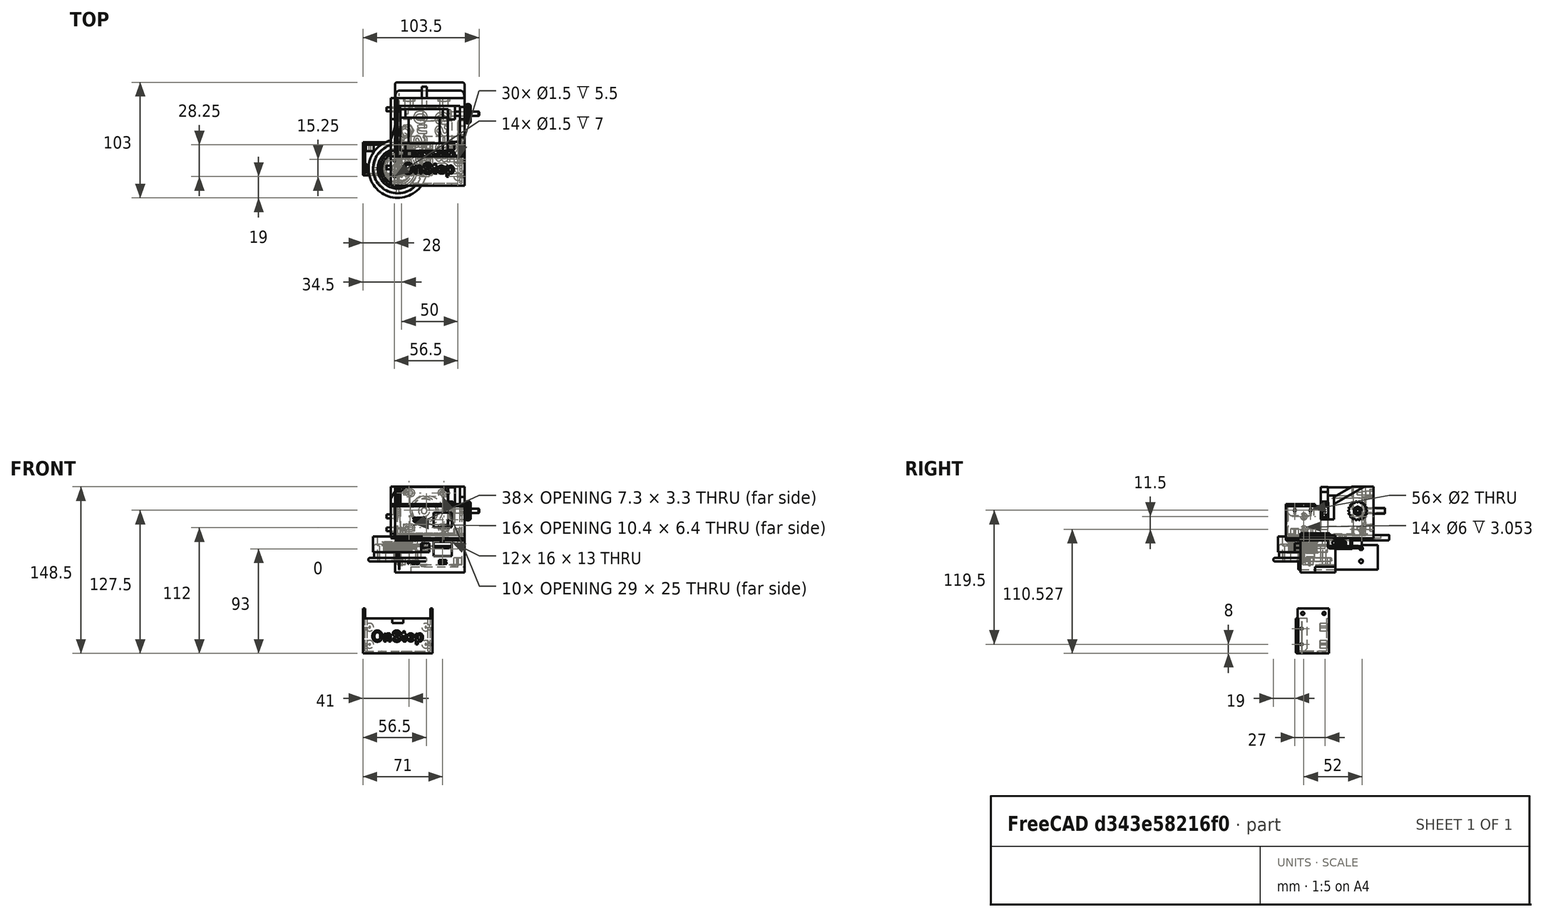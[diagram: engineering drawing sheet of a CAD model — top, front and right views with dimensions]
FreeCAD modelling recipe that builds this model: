
FCSTD DOCUMENT  (FreeCAD 0.17R13387 (Git))
Label: OnStep for GS280
License: All rights reserved
LicenseURL: http://en.wikipedia.org/wiki/All_rights_reserved
objects: Part::Cylinder×217, Part::Box×127, Part::MultiFuse×122, Part::Cut×53, Part::Feature×32, Part::Part2DObjectPython×21, Part::Extrusion×21, Part::FeaturePython×16, Part::Fillet×7, App::Part×6, Mesh::Feature×4, Part::Chamfer×3
note: 619 computed .brp shape members not serialized (recipe doc carries the construction recipe); baked Part::Feature solids carry a one-line shape summary decoded from their .brp

FEATURE [Part::Part2DObjectPython] ShapeString016  # Draft 2D object (typed FeaturePython)
  FontFile = <path>
  Placement = pos=(15.3452,-2,30.5072) rot=(1,0,0;1.5708rad)
  Size = 0.01
  String = .
  Tracking = 0
FEATURE [Part::Part2DObjectPython] ShapeString013  # Draft 2D object (typed FeaturePython)
  FontFile = <path>
  Placement = pos=(15.3452,-2,30.5072) rot=(1,0,0;1.5708rad)
  Size = 10
  String = OnStep
  Tracking = 0
FEATURE [Part::Part2DObjectPython] ShapeString017  # Draft 2D object (typed FeaturePython)
  FontFile = <path>
  Placement = pos=(15.3452,-2,30.5072) rot=(1,0,0;1.5708rad)
  Size = 4
  String = DEC
  Tracking = 0
FEATURE [Part::Cylinder] Cylinder014005703  label="Válec620"
  Angle = 360
  AttacherType = Attacher::AttachEngine3D
  Height = 70
  Placement = pos=(-5,6,16.5) rot=(0,1,0;1.5708rad)
  Radius = 1
FEATURE [Part::Box] Box159  label="Krychle136"
  AttacherType = Attacher::AttachEngine3D
  Height = 2
  Length = 62
  Placement = pos=(-2.5,-2,23) rot=(0,0,1;0rad)
  Width = 31
FEATURE [Part::Box] Box161  label="Krychle138"
  AttacherType = Attacher::AttachEngine3D
  Height = 8
  Length = 58
  Placement = pos=(-0.5,0,15) rot=(0,0,1;0rad)
  Width = 29
FEATURE [Part::MultiFuse] Fusion001071
  Shapes = -> [Box159,Box161]
FEATURE [Part::Box] Box158  label="Krychle135"
  AttacherType = Attacher::AttachEngine3D
  Height = 4
  Length = 10
  Placement = pos=(-5,-8,-55) rot=(0,0,1;0rad)
  Width = 5
FEATURE [Part::Extrusion] Extrude071  label="OnStep005"
  Base = -> ShapeString013
  Dir = (0,-1,0)
  DirMode = 2
  FaceMakerClass = Part::FaceMakerBullseye
  LengthFwd = 1
  LengthRev = 0
  Placement = pos=(-10,-22,22) rot=(-1,0,0;1.5708rad)
  Solid = false
  Symmetric = false
FEATURE [Part::Cylinder] Cylinder014005704  label="Válec621"
  Angle = 360
  AttacherType = Attacher::AttachEngine3D
  Height = 70
  Placement = pos=(-5,20,16.5) rot=(0,1,0;1.5708rad)
  Radius = 1
FEATURE [Part::MultiFuse] Fusion001073  label="Horni diry009"
  Placement = pos=(0,0,3) rot=(0,0,1;0rad)
  Shapes = -> [Cylinder014005704,Cylinder014005703]
FEATURE [Part::Box] Box160  label="Krychle137"
  AttacherType = Attacher::AttachEngine3D
  Height = 8
  Length = 54
  Placement = pos=(1.5,0,15) rot=(0,0,1;0rad)
  Width = 29
FEATURE [Part::MultiFuse] Fusion001072
  Shapes = -> [Fusion001073,Box160]
FEATURE [Part::Cut] Cut061098066
  Base = -> Fusion001071
  Tool = -> Fusion001072
FEATURE [Part::Cut] Cut061098067  label="viko s texty005"
  Base = -> Cut061098066
  Tool = -> Extrude071
FEATURE [Part::Chamfer] Chamfer008017
  Base = -> Cut061098067
  Edges = 2 edges r=2.5: [Edge355,Edge357]
FEATURE [Part::Fillet] Fillet009  label="DEC vicko003"
  Base = -> Chamfer008017
  Edges = 3 edges r=1: [Edge36,Edge38,Edge39]
  Placement = pos=(-28.5,19,-80) rot=(1,0,0;1.5708rad)
FEATURE [Part::Cut] Cut061098065  label="DEC PCB Cap"
  Base = -> Fillet009
  Tool = -> Box158
FEATURE [Part::Extrusion] Extrude086  label="Text RA002"
  Base = -> ShapeString017
  Dir = (0,-1,0)
  DirMode = 2
  FaceMakerClass = Part::FaceMakerBullseye
  LengthFwd = 1
  LengthRev = 0
  Placement = pos=(18,0.5,-33) rot=(0,0,1;0rad)
  Solid = false
  Symmetric = false
FEATURE [Part::Cylinder] Cylinder014005791  label="Válec704"
  Angle = 360
  AttacherType = Attacher::AttachEngine3D
  Height = 70
  Placement = pos=(-5,6,16.5) rot=(0,1,0;1.5708rad)
  Radius = 1
FEATURE [Part::Cylinder] Cylinder014005799  label="Válec712"
  Angle = 360
  AttacherType = Attacher::AttachEngine3D
  Height = 70
  Placement = pos=(-5,20,16.5) rot=(0,1,0;1.5708rad)
  Radius = 1
FEATURE [Part::Cylinder] Cylinder014005792  label="Válec705"
  Angle = 360
  AttacherType = Attacher::AttachEngine3D
  Height = 8
  Placement = pos=(53.5,21.25,0) rot=(0,0,1;0rad)
  Radius = 0.75
FEATURE [Part::Cylinder] Cylinder014005795  label="Válec708"
  Angle = 360
  AttacherType = Attacher::AttachEngine3D
  Height = 6.5
  Placement = pos=(53.5,6,0) rot=(0,0,1;0rad)
  Radius = 3.5
FEATURE [Part::Box] Box203  label="Krychle178"
  AttacherType = Attacher::AttachEngine3D
  Height = 13
  Length = 2
  Placement = pos=(-31,-4.5,-55) rot=(0,0,1;0rad)
  Width = 28
FEATURE [Part::Cylinder] Cylinder014005796  label="Válec709"
  Angle = 360
  AttacherType = Attacher::AttachEngine3D
  Height = 8
  Placement = pos=(53.5,6,0) rot=(0,0,1;0rad)
  Radius = 0.75
FEATURE [Part::Box] Box202  label="Krychle177"
  AttacherType = Attacher::AttachEngine3D
  Height = 13
  Length = 2
  Placement = pos=(29,-4.5,-55) rot=(0,0,1;0rad)
  Width = 28
FEATURE [Part::Box] Box201  label="RJ056"
  AttacherType = Attacher::AttachEngine3D
  Height = 13
  Length = 16
  Placement = pos=(32,-5,4.5) rot=(0,0,1;0rad)
  Width = 18.5
FEATURE [Part::Cylinder] Cylinder014005793  label="Válec706"
  Angle = 360
  AttacherType = Attacher::AttachEngine3D
  Height = 6.5
  Placement = pos=(3.5,21.25,0) rot=(0,0,1;0rad)
  Radius = 3.5
FEATURE [Part::Cylinder] Cylinder014005802  label="Válec715"
  Angle = 360
  AttacherType = Attacher::AttachEngine3D
  Height = 74
  Placement = pos=(-40,19,-46.5) rot=(0,1,0;1.5708rad)
  Radius = 1.4
FEATURE [Part::Box] Box204  label="Krychle179"
  AttacherType = Attacher::AttachEngine3D
  Height = 28
  Length = 62
  Placement = pos=(-2.5,-2,-5) rot=(0,0,1;0rad)
  Width = 31
FEATURE [Part::Box] Box200  label="Krychle176"
  AttacherType = Attacher::AttachEngine3D
  Height = 26
  Length = 58
  Placement = pos=(-0.5,0,-3) rot=(0,0,1;0rad)
  Width = 29
FEATURE [Part::Cut] Cut061098120  label="Základ002"
  Base = -> Box204
  Tool = -> Box200
FEATURE [Part::Extrusion] Extrude087  label="Text TR002"
  Base = -> ShapeString016
  Dir = (0,-1,0)
  DirMode = 2
  FaceMakerClass = Part::FaceMakerBullseye
  LengthFwd = 1
  LengthRev = 0
  Placement = pos=(-6.75,0.5,-33) rot=(0,0,1;0rad)
  Solid = false
  Symmetric = false
FEATURE [Part::Cylinder] Cylinder014005800  label="Válec713"
  Angle = 360
  AttacherType = Attacher::AttachEngine3D
  Height = 8
  Placement = pos=(3.5,21.25,0) rot=(0,0,1;0rad)
  Radius = 0.75
FEATURE [Part::Cylinder] Cylinder014005801  label="Válec714"
  Angle = 360
  AttacherType = Attacher::AttachEngine3D
  Height = 5
  Placement = pos=(14.25,1,9.5) rot=(1,0,0;1.5708rad)
  Radius = 0.01
FEATURE [Part::Cylinder] Cylinder014005803  label="Válec716"
  Angle = 360
  AttacherType = Attacher::AttachEngine3D
  Height = 74
  Placement = pos=(-40,0,-46.5) rot=(0,1,0;1.5708rad)
  Radius = 1.4
FEATURE [Part::Cylinder] Cylinder014005797  label="Válec710"
  Angle = 360
  AttacherType = Attacher::AttachEngine3D
  Height = 6.5
  Placement = pos=(53.5,21.25,0) rot=(0,0,1;0rad)
  Radius = 3.5
FEATURE [Part::Cylinder] Cylinder014005798  label="Válec711"
  Angle = 360
  AttacherType = Attacher::AttachEngine3D
  Height = 8
  Placement = pos=(3.5,6,0) rot=(0,0,1;0rad)
  Radius = 0.7
FEATURE [Part::Cylinder] Cylinder014005794  label="Válec707"
  Angle = 360
  AttacherType = Attacher::AttachEngine3D
  Height = 6.5
  Placement = pos=(3.5,6,0) rot=(0,0,1;0rad)
  Radius = 3.5
FEATURE [Part::MultiFuse] Fusion001089071  label="Horni diry011"
  Placement = pos=(0,0,3) rot=(0,0,1;0rad)
  Shapes = -> [Cylinder014005799,Cylinder014005791]
FEATURE [Part::MultiFuse] Fusion001089075
  Shapes = -> [Extrude087,Extrude086]
FEATURE [Part::MultiFuse] Fusion001089077
  Shapes = -> [Box202,Box203]
FEATURE [Part::MultiFuse] Fusion001089068  label="diry017"
  Placement = pos=(0,0,-4) rot=(0,0,1;0rad)
  Shapes = -> [Cylinder014005800,Cylinder014005798,Cylinder014005792,Cylinder014005796]
FEATURE [Part::MultiFuse] Fusion001089070  label="RJ a LED002"
  Shapes = -> [Box201,Cylinder014005801]
FEATURE [Part::MultiFuse] Fusion001089072  label="sloupky005"
  Placement = pos=(0,0,-3.5) rot=(0,0,1;0rad)
  Shapes = -> [Cylinder014005793,Cylinder014005794,Cylinder014005797,Cylinder014005795]
FEATURE [Part::MultiFuse] Fusion001089073
  Shapes = -> [Cylinder014005803,Cylinder014005802]
FEATURE [Part::MultiFuse] Fusion001089074  label="bez der002"
  Shapes = -> [Cut061098120,Fusion001089072]
FEATURE [Part::MultiFuse] Fusion001089069
  Shapes = -> [Fusion001089068,Fusion001089070,Fusion001089071]
FEATURE [Part::Cut] Cut061098121
  Base = -> Fusion001089074
  Tool = -> Fusion001089069
FEATURE [Part::Cut] Cut061098118
  Base = -> Cut061098121
  Placement = pos=(-28.5,18.5,-80) rot=(1,0,0;1.5708rad)
  Tool = -> Fusion001089075
FEATURE [Part::MultiFuse] Fusion001089076  label="RA pcb box002"
  Shapes = -> [Cut061098118,Fusion001089077]
FEATURE [Part::Cut] Cut061098119  label="DEC PCB BOX For MiniPCB2"
  Base = -> Fusion001089076
  Tool = -> Fusion001089073
FEATURE [Part::Feature] Cut061098127012  label="DE 012"
  shape: bbox 62 x 31 x 33 mm, 80 faces (baked)
FEATURE [Part::Fillet] Fillet004005002  label="DE final"
  Base = -> Cut061098127012
  Edges = 5 edges r=1: [Edge94,Edge95,Edge96,Edge97,Edge98]
FEATURE [Part::Feature] Cut005023015002001  label="RA PCB003"
  shape: bbox 62 x 31 x 33 mm, 145 faces (baked)
FEATURE [App::Part] Part
  Group = -> [Fusion001089075,Fusion001089068,Fusion001089076,Fusion001089077,Fusion001089070,Fusion001089074,Fusion001089069,Fusion001089071,Fusion001089072,Fusion001089073,Cut061098118,Cut061098121,Cut061098120,Cylinder014005802,Box201,Cylinder014005803,Cylinder014005799,Cylinder014005795,Box202,Cylinder014005793,Box203,Extrude086,Cylinder014005791,Box200,Cylinder014005800,Cylinder014005797,Cylinder014005794,+28 more]
  Origin = -> Origin
FEATURE [Mesh::Feature] support_nema17_EQ5_A_D__v1_1  label="support_nema17_EQ5_A.D._v1.1"
FEATURE [Mesh::Feature] support_nema17_EQ5_Dec_v1_1  label="support_nema17_EQ5_Dec_v1.1"
  Placement = pos=(-2,-2,13) rot=(0,0,1;0rad)
FEATURE [Mesh::Feature] holderDEC
  Placement = pos=(0,0,6) rot=(0,0,1;0rad)
FEATURE [Mesh::Feature] holderRA
FEATURE [Part::Feature] Pocket004
  Placement = pos=(22.5,32.5,13.5) rot=(0,0,1;1.5708rad)
  shape: bbox 61 x 74.5 x 11 mm, 39 faces (baked)
FEATURE [Part::Box] Box  label="Krychle"
  AttacherType = Attacher::AttachEngine3D
  Height = 43
  Length = 59.5
  Placement = pos=(0,56,23) rot=(0,0,1;0rad)
  Width = 7
FEATURE [Part::Box] Box205  label="Krychle180"
  AttacherType = Attacher::AttachEngine3D
  Height = 43
  Length = 43
  Placement = pos=(2,53,23) rot=(0,0,1;0rad)
  Width = 3
FEATURE [Part::Cylinder] Cylinder014005804  label="Válec717"
  Angle = 360
  AttacherType = Attacher::AttachEngine3D
  Height = 10
  Placement = pos=(8,57,29.5) rot=(1,0,0;1.5708rad)
  Radius = 1.65
FEATURE [Part::Cylinder] Cylinder014005805  label="Válec718"
  Angle = 360
  AttacherType = Attacher::AttachEngine3D
  Height = 10
  Placement = pos=(39,57,60.5) rot=(1,0,0;1.5708rad)
  Radius = 1.65
FEATURE [Part::Cylinder] Cylinder014005806  label="Válec719"
  Angle = 360
  AttacherType = Attacher::AttachEngine3D
  Height = 10
  Placement = pos=(39,57,29.5) rot=(1,0,0;1.5708rad)
  Radius = 1.65
FEATURE [Part::Cylinder] Cylinder014005807  label="Válec720"
  Angle = 360
  AttacherType = Attacher::AttachEngine3D
  Height = 10
  Placement = pos=(8,57,60.5) rot=(1,0,0;1.5708rad)
  Radius = 1.65
FEATURE [Part::Cylinder] Cylinder014005808  label="Válec721"
  Angle = 360
  AttacherType = Attacher::AttachEngine3D
  Height = 10
  Placement = pos=(23.5,59,45) rot=(1,0,0;1.5708rad)
  Radius = 12.5
FEATURE [Part::Box] Box206  label="Krychle181"
  AttacherType = Attacher::AttachEngine3D
  Height = 43
  Length = 6
  Placement = pos=(45,44,23) rot=(0,0,1;0rad)
  Width = 12
FEATURE [Part::FeaturePython] Screw010  label="M4x25-Screw001"  # Fasteners workbench fastener (typed FeaturePython)
  Placement = pos=(47.5,49,45) rot=(0,-1,0;1.5708rad)
  diameter = 6
  invert = false
  length = 0
  matchOuter = false
  offset = 0
  thread = false
  type = 13
FEATURE [Part::MultiFuse] Fusion  label="diry jezdec"
  Shapes = -> [Cylinder014005804,Cylinder014005808,Cylinder014005807,Cylinder014005806,Cylinder014005805,Screw010]
FEATURE [Part::MultiFuse] Fusion001089078
  Shapes = -> [Box205,Box206]
FEATURE [Part::Cut] Cut  label="Jezdec"
  Base = -> Fusion001089078
  Tool = -> Fusion
FEATURE [Part::Cylinder] Cylinder014005809  label="Válec722"
  Angle = 360
  AttacherType = Attacher::AttachEngine3D
  Height = 20
  Placement = pos=(23.5,64,45) rot=(1,0,0;1.5708rad)
  Radius = 12.5
FEATURE [Part::Cylinder] Cylinder014005810  label="Válec723"
  Angle = 360
  AttacherType = Attacher::AttachEngine3D
  Height = 10
  Placement = pos=(8,64,29.5) rot=(1,0,0;1.5708rad)
  Radius = 1.65
FEATURE [Part::Cylinder] Cylinder014005811  label="Válec724"
  Angle = 360
  AttacherType = Attacher::AttachEngine3D
  Height = 10
  Placement = pos=(8,64,60.5) rot=(1,0,0;1.5708rad)
  Radius = 1.65
FEATURE [Part::Cylinder] Cylinder014005812  label="Válec725"
  Angle = 360
  AttacherType = Attacher::AttachEngine3D
  Height = 10
  Placement = pos=(39,64,29.5) rot=(1,0,0;1.5708rad)
  Radius = 1.65
FEATURE [Part::Cylinder] Cylinder014005813  label="Válec726"
  Angle = 360
  AttacherType = Attacher::AttachEngine3D
  Height = 10
  Placement = pos=(39,64,60.5) rot=(1,0,0;1.5708rad)
  Radius = 1.65
FEATURE [Part::FeaturePython] Screw011  label="M4x25-Screw002"  # Fasteners workbench fastener (typed FeaturePython)
  Placement = pos=(47.5,49,45) rot=(0,-1,0;1.5708rad)
  diameter = 6
  invert = false
  length = 0
  matchOuter = false
  offset = 0
  thread = false
  type = 13
FEATURE [Part::Box] Box207  label="Krychle182"
  AttacherType = Attacher::AttachEngine3D
  Height = 43
  Length = 4
  Placement = pos=(55.5,16,23) rot=(0,0,1;0rad)
  Width = 40
FEATURE [Part::Cylinder] Cylinder014005814  label="Válec727"
  Angle = 360
  AttacherType = Attacher::AttachEngine3D
  Height = 10
  Placement = pos=(8,64,29.5) rot=(1,0,0;1.5708rad)
  Radius = 1.65
FEATURE [Part::Cylinder] Cylinder014005815  label="Válec728"
  Angle = 360
  AttacherType = Attacher::AttachEngine3D
  Height = 20
  Placement = pos=(23.5,64,45) rot=(1,0,0;1.5708rad)
  Radius = 12.5
FEATURE [Part::Cylinder] Cylinder014005816  label="Válec729"
  Angle = 360
  AttacherType = Attacher::AttachEngine3D
  Height = 10
  Placement = pos=(8,64,60.5) rot=(1,0,0;1.5708rad)
  Radius = 1.65
FEATURE [Part::Cylinder] Cylinder014005817  label="Válec730"
  Angle = 360
  AttacherType = Attacher::AttachEngine3D
  Height = 10
  Placement = pos=(39,64,29.5) rot=(1,0,0;1.5708rad)
  Radius = 1.65
FEATURE [Part::Cylinder] Cylinder014005818  label="Válec731"
  Angle = 360
  AttacherType = Attacher::AttachEngine3D
  Height = 10
  Placement = pos=(39,64,60.5) rot=(1,0,0;1.5708rad)
  Radius = 1.65
FEATURE [Part::MultiFuse] Fusion001089080
  Placement = pos=(4,0,0) rot=(0,0,1;0rad)
  Shapes = -> [Cylinder014005814,Cylinder014005816,Cylinder014005818,Cylinder014005815,Cylinder014005817]
FEATURE [Part::Box] Box208  label="Krychle183"
  AttacherType = Attacher::AttachEngine3D
  Height = 25
  Length = 4
  Placement = pos=(23.5,56,32.5) rot=(0,0,1;0rad)
  Width = 8
FEATURE [Part::Box] Box209  label="Krychle184"
  AttacherType = Attacher::AttachEngine3D
  Height = 3.3
  Length = 4
  Placement = pos=(8,56,27.85) rot=(0,0,1;0rad)
  Width = 8
FEATURE [Part::Box] Box210  label="Krychle185"
  AttacherType = Attacher::AttachEngine3D
  Height = 3.3
  Length = 4
  Placement = pos=(39,56,58.85) rot=(0,0,1;0rad)
  Width = 8
FEATURE [Part::Box] Box211  label="Krychle186"
  AttacherType = Attacher::AttachEngine3D
  Height = 3.3
  Length = 4
  Placement = pos=(39,56,27.85) rot=(0,0,1;0rad)
  Width = 8
FEATURE [Part::Box] Box212  label="Krychle187"
  AttacherType = Attacher::AttachEngine3D
  Height = 3.3
  Length = 4
  Placement = pos=(8,56,58.85) rot=(0,0,1;0rad)
  Width = 8
FEATURE [Part::MultiFuse] Fusion001089081  label="Main"
  Placement = pos=(0,0,0.5) rot=(0,0,1;0rad)
  Shapes = -> [Box,Box207]
FEATURE [Part::Box] Box213  label="konektor"
  AttacherType = Attacher::AttachEngine3D
  Height = 29
  Length = 10
  Placement = pos=(50,16,37) rot=(0,0,1;0rad)
  Width = 12
FEATURE [Part::Box] Box214  label="Krychle188"
  AttacherType = Attacher::AttachEngine3D
  Height = 43
  Length = 4
  Placement = pos=(55.5,22,47) rot=(1,0,0;0.523599rad)
  Width = 40
FEATURE [Part::MultiFuse] Fusion001089079  label="diry"
  Placement = pos=(0,0,0.5) rot=(0,0,1;0rad)
  Shapes = -> [Cylinder014005810,Cylinder014005809,Cylinder014005811,Cylinder014005812,Cylinder014005813,Screw011,Fusion001089080,Box208,Box209,Box210,Box211,Box212,Box213,Box214]
FEATURE [Part::Cut] Cut005023015002002  label="RA"
  Base = -> Fusion001089081
  Tool = -> Fusion001089079
FEATURE [Part::Part2DObjectPython] ShapeString015  # Draft 2D object (typed FeaturePython)
  FontFile = <path>
  Placement = pos=(15.3452,-2,30.5072) rot=(1,0,0;1.5708rad)
  Size = 0.01
  String = .
  Tracking = 0
FEATURE [Part::Part2DObjectPython] ShapeString014  # Draft 2D object (typed FeaturePython)
  FontFile = <path>
  Placement = pos=(15.3452,-2,30.5072) rot=(1,0,0;1.5708rad)
  Size = 4
  String = RA
  Tracking = 0
FEATURE [Part::Cylinder] Cylinder014005783  label="Válec696"
  Angle = 360
  AttacherType = Attacher::AttachEngine3D
  Height = 70
  Placement = pos=(-5,20,16.5) rot=(0,1,0;1.5708rad)
  Radius = 1
FEATURE [Part::Extrusion] Extrude084  label="Text RA001"
  Base = -> ShapeString014
  Dir = (0,-1,0)
  DirMode = 2
  FaceMakerClass = Part::FaceMakerBullseye
  LengthFwd = 1
  LengthRev = 0
  Placement = pos=(4,0.7,-23.5) rot=(0,0,1;0rad)
  Solid = false
  Symmetric = false
FEATURE [Part::Cylinder] Cylinder014005778  label="Válec691"
  Angle = 360
  AttacherType = Attacher::AttachEngine3D
  Height = 8
  Placement = pos=(3.5,6,0) rot=(0,0,1;0rad)
  Radius = 0.7
FEATURE [Part::Cylinder] Cylinder014005779  label="Válec692"
  Angle = 360
  AttacherType = Attacher::AttachEngine3D
  Height = 8
  Placement = pos=(53.5,21.25,0) rot=(0,0,1;0rad)
  Radius = 0.75
FEATURE [Part::Cylinder] Cylinder014005780  label="Válec693"
  Angle = 360
  AttacherType = Attacher::AttachEngine3D
  Height = 6.5
  Placement = pos=(3.5,6,0) rot=(0,0,1;0rad)
  Radius = 3.5
FEATURE [Part::Box] Box195  label="Krychle172"
  AttacherType = Attacher::AttachEngine3D
  Height = 26
  Length = 58
  Placement = pos=(-0.5,0,-3) rot=(0,0,1;0rad)
  Width = 29
FEATURE [Part::Cylinder] Cylinder014005781  label="Válec694"
  Angle = 360
  AttacherType = Attacher::AttachEngine3D
  Height = 6.5
  Placement = pos=(53.5,21.25,0) rot=(0,0,1;0rad)
  Radius = 3.5
FEATURE [Part::Cylinder] Cylinder014005782  label="Válec695"
  Angle = 360
  AttacherType = Attacher::AttachEngine3D
  Height = 8
  Placement = pos=(53.5,6,0) rot=(0,0,1;0rad)
  Radius = 0.75
FEATURE [Part::Cylinder] Cylinder014005784  label="Válec697"
  Angle = 360
  AttacherType = Attacher::AttachEngine3D
  Height = 70
  Placement = pos=(-5,6,16.5) rot=(0,1,0;1.5708rad)
  Radius = 1
FEATURE [Part::Box] Box196  label="RJ055"
  AttacherType = Attacher::AttachEngine3D
  Height = 13
  Length = 16
  Placement = pos=(32,-5,4.5) rot=(0,0,1;0rad)
  Width = 18.5
FEATURE [Part::Cylinder] Cylinder014005786  label="Válec699"
  Angle = 360
  AttacherType = Attacher::AttachEngine3D
  Height = 8
  Placement = pos=(3.5,21.25,0) rot=(0,0,1;0rad)
  Radius = 0.75
FEATURE [Part::Cylinder] Cylinder014005787  label="Válec700"
  Angle = 360
  AttacherType = Attacher::AttachEngine3D
  Height = 6.5
  Placement = pos=(3.5,21.25,0) rot=(0,0,1;0rad)
  Radius = 3.5
FEATURE [Part::Cylinder] Cylinder014005785  label="Válec698"
  Angle = 360
  AttacherType = Attacher::AttachEngine3D
  Height = 5
  Placement = pos=(14.25,1,9.5) rot=(1,0,0;1.5708rad)
  Radius = 0.01
FEATURE [Part::Cylinder] Cylinder014005788  label="Válec701"
  Angle = 360
  AttacherType = Attacher::AttachEngine3D
  Height = 6.5
  Placement = pos=(53.5,6,0) rot=(0,0,1;0rad)
  Radius = 3.5
FEATURE [Part::Box] Box199  label="Krychle175"
  AttacherType = Attacher::AttachEngine3D
  Height = 28
  Length = 62
  Placement = pos=(-2.5,-2,-5) rot=(0,0,1;0rad)
  Width = 31
FEATURE [Part::Cut] Cut061098114  label="Základ001"
  Base = -> Box199
  Tool = -> Box195
FEATURE [Part::Extrusion] Extrude085  label="Text TR001"
  Base = -> ShapeString015
  Dir = (0,-1,0)
  DirMode = 2
  FaceMakerClass = Part::FaceMakerBullseye
  LengthFwd = 1
  LengthRev = 0
  Placement = pos=(-6.75,1,-33) rot=(0,0,1;0rad)
  Solid = false
  Symmetric = false
FEATURE [Part::MultiFuse] Fusion001089063
  Shapes = -> [Extrude085,Extrude084]
FEATURE [Part::MultiFuse] Fusion001089058  label="RJ a LED001"
  Shapes = -> [Box196,Cylinder014005785]
FEATURE [Part::MultiFuse] Fusion001089059  label="Horni diry010"
  Placement = pos=(0,0,3) rot=(0,0,1;0rad)
  Shapes = -> [Cylinder014005783,Cylinder014005784]
FEATURE [Part::MultiFuse] Fusion001089060  label="diry016"
  Placement = pos=(0,0,-4) rot=(0,0,1;0rad)
  Shapes = -> [Cylinder014005786,Cylinder014005778,Cylinder014005779,Cylinder014005782]
FEATURE [Part::MultiFuse] Fusion001089062
  Shapes = -> [Fusion001089060,Fusion001089058,Fusion001089059]
FEATURE [Part::MultiFuse] Fusion001089061  label="sloupky004"
  Placement = pos=(0,0,-3.5) rot=(0,0,1;0rad)
  Shapes = -> [Cylinder014005787,Cylinder014005780,Cylinder014005781,Cylinder014005788]
FEATURE [Part::MultiFuse] Fusion001089067  label="bez der001"
  Shapes = -> [Cut061098114,Fusion001089061]
FEATURE [Part::Cut] Cut061098117
  Base = -> Fusion001089067
  Tool = -> Fusion001089062
FEATURE [Part::Cut] Cut061098115  label="PCB"
  Base = -> Cut061098117
  Placement = pos=(0,-13,26) rot=(1,0,0;0rad)
  Tool = -> Fusion001089063
FEATURE [Part::Box] Box215  label="Krychle189"
  AttacherType = Attacher::AttachEngine3D
  Height = 3
  Length = 62
  Placement = pos=(-2.5,-15,20.5) rot=(0,0,1;0rad)
  Width = 78
FEATURE [Part::Box] Box216  label="Krychle190"
  AttacherType = Attacher::AttachEngine3D
  Height = 8
  Length = 24
  Placement = pos=(-1.5,12.5,13.5) rot=(0,0,1;0rad)
  Width = 40
FEATURE [Part::Box] Box217  label="Krychle191"
  AttacherType = Attacher::AttachEngine3D
  Height = 8
  Length = 26
  Placement = pos=(22.5,22.5,13.5) rot=(0,0,1;0rad)
  Width = 20
FEATURE [Part::Box] Box218  label="Krychle192"
  AttacherType = Attacher::AttachEngine3D
  Height = 8
  Length = 6
  Placement = pos=(53.5,22.5,13.5) rot=(0,0,1;0rad)
  Width = 20
FEATURE [Part::MultiFuse] Fusion001089082  label="spodek"
  Shapes = -> [Box215,Box218,Box216,Box217]
FEATURE [Part::FeaturePython] Screw  label="M6x12-Screw"  # Fasteners workbench fastener (typed FeaturePython)
  Placement = pos=(6.5,32.5,19.5) rot=(1,0,0;0rad)
  diameter = 8
  invert = false
  length = 0
  matchOuter = false
  offset = 0
  thread = false
  type = 14
FEATURE [Part::Cylinder] Cylinder  label="Válec"
  Angle = 360
  AttacherType = Attacher::AttachEngine3D
  Height = 10
  Placement = pos=(52,28,16.5) rot=(0,1,0;1.5708rad)
  Radius = 1.65
FEATURE [Part::Cylinder] Cylinder014005819  label="Válec732"
  Angle = 360
  AttacherType = Attacher::AttachEngine3D
  Height = 10
  Placement = pos=(52,37,16.5) rot=(0,1,0;1.5708rad)
  Radius = 1.65
FEATURE [Part::Box] Box219  label="Krychle193"
  AttacherType = Attacher::AttachEngine3D
  Height = 3.3
  Length = 10
  Placement = pos=(52,28,14.85) rot=(0,0,1;0rad)
  Width = 9
FEATURE [Part::MultiFuse] Fusion001089083  label="Diryspodek"
  Shapes = -> [Box219,Cylinder,Cylinder014005819,Screw]
FEATURE [Part::Cut] Cut005023015002003  label="Spodek"
  Base = -> Fusion001089082
  Tool = -> Fusion001089083
FEATURE [Part::MultiFuse] Fusion001089084
  Shapes = -> [Cut061098115,Cut005023015002003,Cut005023015002002]
FEATURE [Part::FeaturePython] Screw012  label="M4x25-Screw003"  # Fasteners workbench fastener (typed FeaturePython)
  Placement = pos=(47.5,49,45) rot=(0,-1,0;1.5708rad)
  diameter = 6
  invert = false
  length = 0
  matchOuter = false
  offset = 0
  thread = false
  type = 13
FEATURE [Part::FeaturePython] Screw013  label="M6x12-Screw001"  # Fasteners workbench fastener (typed FeaturePython)
  Placement = pos=(8.5,34,19.5) rot=(1,0,0;0rad)
  diameter = 8
  invert = false
  length = 0
  matchOuter = false
  offset = 0
  thread = false
  type = 14
FEATURE [Part::Cylinder] Cylinder014005820  label="Válec733"
  Angle = 360
  AttacherType = Attacher::AttachEngine3D
  Height = 10
  Placement = pos=(8,64,60.5) rot=(1,0,0;1.5708rad)
  Radius = 1.65
FEATURE [Part::Cylinder] Cylinder014005821  label="Válec734"
  Angle = 360
  AttacherType = Attacher::AttachEngine3D
  Height = 10
  Placement = pos=(39,64,29.5) rot=(1,0,0;1.5708rad)
  Radius = 1.65
FEATURE [Part::Cylinder] Cylinder014005822  label="Válec735"
  Angle = 360
  AttacherType = Attacher::AttachEngine3D
  Height = 10
  Placement = pos=(8,64,60.5) rot=(1,0,0;1.5708rad)
  Radius = 1.65
FEATURE [Part::Cylinder] Cylinder014005823  label="Válec736"
  Angle = 360
  AttacherType = Attacher::AttachEngine3D
  Height = 10
  Placement = pos=(8,64,29.5) rot=(1,0,0;1.5708rad)
  Radius = 1.65
FEATURE [Part::Cylinder] Cylinder014005824  label="Válec737"
  Angle = 360
  AttacherType = Attacher::AttachEngine3D
  Height = 10
  Placement = pos=(39,64,29.5) rot=(1,0,0;1.5708rad)
  Radius = 1.65
FEATURE [Part::Box] Box220  label="Krychle194"
  AttacherType = Attacher::AttachEngine3D
  Height = 43
  Length = 59.5
  Placement = pos=(0,56,23) rot=(0,0,1;0rad)
  Width = 7
FEATURE [Part::Box] Box221  label="Krychle195"
  AttacherType = Attacher::AttachEngine3D
  Height = 43
  Length = 4
  Placement = pos=(55.5,16,23) rot=(0,0,1;0rad)
  Width = 40
FEATURE [Part::Cylinder] Cylinder014005825  label="Válec738"
  Angle = 360
  AttacherType = Attacher::AttachEngine3D
  Height = 20
  Placement = pos=(23.5,64,45) rot=(1,0,0;1.5708rad)
  Radius = 12.5
FEATURE [Part::Cylinder] Cylinder014005826  label="Válec739"
  Angle = 360
  AttacherType = Attacher::AttachEngine3D
  Height = 10
  Placement = pos=(39,64,60.5) rot=(1,0,0;1.5708rad)
  Radius = 1.65
FEATURE [Part::Cylinder] Cylinder014005827  label="Válec740"
  Angle = 360
  AttacherType = Attacher::AttachEngine3D
  Height = 10
  Placement = pos=(8,64,29.5) rot=(1,0,0;1.5708rad)
  Radius = 1.65
FEATURE [Part::Cylinder] Cylinder014005828  label="Válec741"
  Angle = 360
  AttacherType = Attacher::AttachEngine3D
  Height = 20
  Placement = pos=(23.5,64,45) rot=(1,0,0;1.5708rad)
  Radius = 12.5
FEATURE [Part::MultiFuse] Fusion001089085  label="Main001"
  Placement = pos=(0,0,0.5) rot=(0,0,1;0rad)
  Shapes = -> [Box220,Box221]
FEATURE [Part::Cylinder] Cylinder014005829  label="Válec742"
  Angle = 360
  AttacherType = Attacher::AttachEngine3D
  Height = 10
  Placement = pos=(39,64,60.5) rot=(1,0,0;1.5708rad)
  Radius = 1.65
FEATURE [Part::MultiFuse] Fusion001089090
  Placement = pos=(4,0,0) rot=(0,0,1;0rad)
  Shapes = -> [Cylinder014005827,Cylinder014005820,Cylinder014005829,Cylinder014005828,Cylinder014005821]
FEATURE [Part::Box] Box224  label="Krychle198"
  AttacherType = Attacher::AttachEngine3D
  Height = 9
  Length = 26
  Placement = pos=(-2,24,13) rot=(0,0,1;0rad)
  Width = 20
FEATURE [Part::Box] Box225  label="Krychle199"
  AttacherType = Attacher::AttachEngine3D
  Height = 25
  Length = 4
  Placement = pos=(23.5,56,32.5) rot=(0,0,1;0rad)
  Width = 8
FEATURE [Part::Box] Box226  label="Krychle200"
  AttacherType = Attacher::AttachEngine3D
  Height = 3.3
  Length = 4
  Placement = pos=(39,56,58.85) rot=(0,0,1;0rad)
  Width = 8
FEATURE [Part::Box] Box227  label="Krychle201"
  AttacherType = Attacher::AttachEngine3D
  Height = 43
  Length = 4
  Placement = pos=(55.5,22,47) rot=(1,0,0;0.523599rad)
  Width = 40
FEATURE [Part::Box] Box228  label="konektor001"
  AttacherType = Attacher::AttachEngine3D
  Height = 29
  Length = 10
  Placement = pos=(50,16,37) rot=(0,0,1;0rad)
  Width = 12
FEATURE [Part::Box] Box229  label="Krychle202"
  AttacherType = Attacher::AttachEngine3D
  Height = 3.3
  Length = 4
  Placement = pos=(39,56,27.85) rot=(0,0,1;0rad)
  Width = 8
FEATURE [Part::Box] Box230  label="Krychle203"
  AttacherType = Attacher::AttachEngine3D
  Height = 3.3
  Length = 4
  Placement = pos=(8,56,27.85) rot=(0,0,1;0rad)
  Width = 8
FEATURE [Part::Box] Box232  label="Krychle204"
  AttacherType = Attacher::AttachEngine3D
  Height = 3
  Length = 62
  Placement = pos=(-2.5,-15,20.5) rot=(0,0,1;0rad)
  Width = 78
FEATURE [Part::MultiFuse] Fusion001089088  label="spodek001"
  Shapes = -> [Box232,Box224]
FEATURE [Part::Box] Box233  label="Krychle205"
  AttacherType = Attacher::AttachEngine3D
  Height = 3.3
  Length = 4
  Placement = pos=(8,56,58.85) rot=(0,0,1;0rad)
  Width = 8
FEATURE [Part::MultiFuse] Fusion001089091  label="diry018"
  Placement = pos=(0,0,0.5) rot=(0,0,1;0rad)
  Shapes = -> [Cylinder014005823,Cylinder014005825,Cylinder014005822,Cylinder014005824,Cylinder014005826,Screw012,Fusion001089090,Box225,Box230,Box226,Box229,Box233,Box228,Box227]
FEATURE [Part::Cut] Cut005023015002008  label="DEC"
  Base = -> Fusion001089085
  Tool = -> Fusion001089091
FEATURE [Part::Cut] Cut005023015002009  label="dec spodek"
  Base = -> Fusion001089088
  Tool = -> Screw013
FEATURE [Part::Part2DObjectPython] ShapeString018  # Draft 2D object (typed FeaturePython)
  FontFile = <path>
  Placement = pos=(15.3452,-2,30.5072) rot=(1,0,0;1.5708rad)
  Size = 4
  String = DEC
  Tracking = 0
FEATURE [Part::Part2DObjectPython] ShapeString019  # Draft 2D object (typed FeaturePython)
  FontFile = <path>
  Placement = pos=(15.3452,-2,30.5072) rot=(1,0,0;1.5708rad)
  Size = 0.01
  String = .
  Tracking = 0
FEATURE [Part::Box] Box234  label="Krychle206"
  AttacherType = Attacher::AttachEngine3D
  Height = 26
  Length = 58
  Placement = pos=(-0.5,0,-3) rot=(0,0,1;0rad)
  Width = 29
FEATURE [Part::Box] Box235  label="Krychle207"
  AttacherType = Attacher::AttachEngine3D
  Height = 28
  Length = 62
  Placement = pos=(-2.5,-2,-5) rot=(0,0,1;0rad)
  Width = 31
FEATURE [Part::Cut] Cut005023015002010  label="Základ003"
  Base = -> Box235
  Tool = -> Box234
FEATURE [Part::Cylinder] Cylinder014005830  label="Válec743"
  Angle = 360
  AttacherType = Attacher::AttachEngine3D
  Height = 70
  Placement = pos=(-5,20,16.5) rot=(0,1,0;1.5708rad)
  Radius = 1
FEATURE [Part::Extrusion] Extrude088  label="Text TR003"
  Base = -> ShapeString019
  Dir = (0,-1,0)
  DirMode = 2
  FaceMakerClass = Part::FaceMakerBullseye
  LengthFwd = 1
  LengthRev = 0
  Placement = pos=(-6.75,0.5,-33) rot=(0,0,1;0rad)
  Solid = false
  Symmetric = false
FEATURE [Part::Cylinder] Cylinder014005831  label="Válec744"
  Angle = 360
  AttacherType = Attacher::AttachEngine3D
  Height = 8
  Placement = pos=(3.5,6,0) rot=(0,0,1;0rad)
  Radius = 0.7
FEATURE [Part::Cylinder] Cylinder014005832  label="Válec745"
  Angle = 360
  AttacherType = Attacher::AttachEngine3D
  Height = 8
  Placement = pos=(53.5,21.25,0) rot=(0,0,1;0rad)
  Radius = 0.75
FEATURE [Part::Cylinder] Cylinder014005833  label="Válec746"
  Angle = 360
  AttacherType = Attacher::AttachEngine3D
  Height = 6.5
  Placement = pos=(3.5,6,0) rot=(0,0,1;0rad)
  Radius = 3.5
FEATURE [Part::Cylinder] Cylinder014005834  label="Válec747"
  Angle = 360
  AttacherType = Attacher::AttachEngine3D
  Height = 6.5
  Placement = pos=(53.5,21.25,0) rot=(0,0,1;0rad)
  Radius = 3.5
FEATURE [Part::Cylinder] Cylinder014005835  label="Válec748"
  Angle = 360
  AttacherType = Attacher::AttachEngine3D
  Height = 8
  Placement = pos=(53.5,6,0) rot=(0,0,1;0rad)
  Radius = 0.75
FEATURE [Part::Cylinder] Cylinder014005836  label="Válec749"
  Angle = 360
  AttacherType = Attacher::AttachEngine3D
  Height = 70
  Placement = pos=(-5,6,16.5) rot=(0,1,0;1.5708rad)
  Radius = 1
FEATURE [Part::MultiFuse] Fusion001089097  label="Horni diry012"
  Placement = pos=(0,0,3) rot=(0,0,1;0rad)
  Shapes = -> [Cylinder014005830,Cylinder014005836]
FEATURE [Part::Extrusion] Extrude089  label="Text RA003"
  Base = -> ShapeString018
  Dir = (0,-1,0)
  DirMode = 2
  FaceMakerClass = Part::FaceMakerBullseye
  LengthFwd = 1
  LengthRev = 0
  Placement = pos=(40,1,43.5) rot=(0,1,0;3.14159rad)
  Solid = false
  Symmetric = false
FEATURE [Part::MultiFuse] Fusion001089095
  Shapes = -> [Extrude088,Extrude089]
FEATURE [Part::Box] Box236  label="RJ057"
  AttacherType = Attacher::AttachEngine3D
  Height = 13
  Length = 16
  Placement = pos=(32,-5,4.5) rot=(0,0,1;0rad)
  Width = 18.5
FEATURE [Part::Cylinder] Cylinder014005837  label="Válec750"
  Angle = 360
  AttacherType = Attacher::AttachEngine3D
  Height = 8
  Placement = pos=(3.5,21.25,0) rot=(0,0,1;0rad)
  Radius = 0.75
FEATURE [Part::MultiFuse] Fusion001089098  label="diry019"
  Placement = pos=(0,0,-4) rot=(0,0,1;0rad)
  Shapes = -> [Cylinder014005837,Cylinder014005831,Cylinder014005832,Cylinder014005835]
FEATURE [Part::Cylinder] Cylinder014005838  label="Válec751"
  Angle = 360
  AttacherType = Attacher::AttachEngine3D
  Height = 6.5
  Placement = pos=(3.5,21.25,0) rot=(0,0,1;0rad)
  Radius = 3.5
FEATURE [Part::Cylinder] Cylinder014005839  label="Válec752"
  Angle = 360
  AttacherType = Attacher::AttachEngine3D
  Height = 5
  Placement = pos=(14.25,1,9.5) rot=(1,0,0;1.5708rad)
  Radius = 0.01
FEATURE [Part::MultiFuse] Fusion001089096  label="RJ a LED003"
  Shapes = -> [Box236,Cylinder014005839]
FEATURE [Part::MultiFuse] Fusion001089092
  Shapes = -> [Fusion001089098,Fusion001089096,Fusion001089097]
FEATURE [Part::Cylinder] Cylinder014005840  label="Válec753"
  Angle = 360
  AttacherType = Attacher::AttachEngine3D
  Height = 6.5
  Placement = pos=(53.5,6,0) rot=(0,0,1;0rad)
  Radius = 3.5
FEATURE [Part::MultiFuse] Fusion001089093  label="sloupky006"
  Placement = pos=(0,0,-3.5) rot=(0,0,1;0rad)
  Shapes = -> [Cylinder014005838,Cylinder014005833,Cylinder014005834,Cylinder014005840]
FEATURE [Part::MultiFuse] Fusion001089094  label="bez der003"
  Shapes = -> [Cut005023015002010,Fusion001089093]
FEATURE [Part::Cut] Cut005023015002011
  Base = -> Fusion001089094
  Tool = -> Fusion001089092
FEATURE [Part::Cut] Cut005023015002012  label="PCB001"
  Base = -> Cut005023015002011
  Placement = pos=(0,-13,26) rot=(1,0,0;0rad)
  Tool = -> Fusion001089095
FEATURE [Part::MultiFuse] Fusion001089099  label="Dec-fin"
  Shapes = -> [Cut005023015002012,Cut005023015002008,Cut005023015002009]
FEATURE [Part::Fillet] Fillet  label="RAv1"
  Base = -> Fusion001089084
  Edges = 2 edges r=2: [Edge279,Edge287]
FEATURE [Part::Part2DObjectPython] ShapeString020  # Draft 2D object (typed FeaturePython)
  FontFile = <path>
  Placement = pos=(15.3452,-2,30.5072) rot=(1,0,0;1.5708rad)
  Size = 0.01
  String = .
  Tracking = 0
FEATURE [Part::Extrusion] Extrude091  label="Text TR004"
  Base = -> ShapeString020
  Dir = (0,-1,0)
  DirMode = 2
  FaceMakerClass = Part::FaceMakerBullseye
  LengthFwd = 1
  LengthRev = 0
  Placement = pos=(-6.75,1,-33) rot=(0,0,1;0rad)
  Solid = false
  Symmetric = false
FEATURE [Part::Box] Box237  label="Krychle208"
  AttacherType = Attacher::AttachEngine3D
  Height = 43
  Length = 59.5
  Placement = pos=(0,56,23) rot=(0,0,1;0rad)
  Width = 7
FEATURE [Part::FeaturePython] Screw014  label="M6x12-Screw002"  # Fasteners workbench fastener (typed FeaturePython)
  Placement = pos=(6.5,32.5,20.5) rot=(1,0,0;0rad)
  diameter = 8
  invert = false
  length = 0
  matchOuter = false
  offset = 0
  thread = false
  type = 14
FEATURE [Part::FeaturePython] Screw015  label="M4x25-Screw004"  # Fasteners workbench fastener (typed FeaturePython)
  Placement = pos=(47.5,49,45) rot=(0,-1,0;1.5708rad)
  diameter = 6
  invert = false
  length = 0
  matchOuter = false
  offset = 0
  thread = false
  type = 13
FEATURE [Part::Part2DObjectPython] ShapeString021  # Draft 2D object (typed FeaturePython)
  FontFile = <path>
  Placement = pos=(15.3452,-2,30.5072) rot=(1,0,0;1.5708rad)
  Size = 4
  String = RA
  Tracking = 0
FEATURE [Part::Extrusion] Extrude090  label="Text RA004"
  Base = -> ShapeString021
  Dir = (0,-1,0)
  DirMode = 2
  FaceMakerClass = Part::FaceMakerBullseye
  LengthFwd = 1
  LengthRev = 0
  Placement = pos=(4,0.7,-23.5) rot=(0,0,1;0rad)
  Solid = false
  Symmetric = false
FEATURE [Part::MultiFuse] Fusion001089103
  Shapes = -> [Extrude091,Extrude090]
FEATURE [Part::Box] Box238  label="Krychle209"
  AttacherType = Attacher::AttachEngine3D
  Height = 3.3
  Length = 4
  Placement = pos=(39,56,58.85) rot=(0,0,1;0rad)
  Width = 8
FEATURE [Part::Cylinder] Cylinder014005841  label="Válec754"
  Angle = 360
  AttacherType = Attacher::AttachEngine3D
  Height = 6.5
  Placement = pos=(53.5,21.25,0) rot=(0,0,1;0rad)
  Radius = 3.5
FEATURE [Part::Cylinder] Cylinder014005842  label="Válec755"
  Angle = 360
  AttacherType = Attacher::AttachEngine3D
  Height = 10
  Placement = pos=(8,64,60.5) rot=(1,0,0;1.5708rad)
  Radius = 1.65
FEATURE [Part::Cylinder] Cylinder014005843  label="Válec756"
  Angle = 360
  AttacherType = Attacher::AttachEngine3D
  Height = 20
  Placement = pos=(23.5,64,45) rot=(1,0,0;1.5708rad)
  Radius = 12.5
FEATURE [Part::Box] Box239  label="konektor002"
  AttacherType = Attacher::AttachEngine3D
  Height = 29
  Length = 10
  Placement = pos=(50,16,37) rot=(0,0,1;0rad)
  Width = 12
FEATURE [Part::Box] Box240  label="Krychle210"
  AttacherType = Attacher::AttachEngine3D
  Height = 43
  Length = 65
  Placement = pos=(-5,15.5,49.5) rot=(1,0,0;0.523599rad)
  Width = 48
FEATURE [Part::Cylinder] Cylinder014005844  label="Válec757"
  Angle = 360
  AttacherType = Attacher::AttachEngine3D
  Height = 10
  Placement = pos=(8,64,29.5) rot=(1,0,0;1.5708rad)
  Radius = 1.65
FEATURE [Part::Cylinder] Cylinder014005845  label="Válec758"
  Angle = 360
  AttacherType = Attacher::AttachEngine3D
  Height = 10
  Placement = pos=(39,64,29.5) rot=(1,0,0;1.5708rad)
  Radius = 1.65
FEATURE [Part::Box] Box241  label="Krychle211"
  AttacherType = Attacher::AttachEngine3D
  Height = 43
  Length = 4
  Placement = pos=(55.5,16,23) rot=(0,0,1;0rad)
  Width = 40
FEATURE [Part::Cylinder] Cylinder014005846  label="Válec759"
  Angle = 360
  AttacherType = Attacher::AttachEngine3D
  Height = 10
  Placement = pos=(8,64,29.5) rot=(1,0,0;1.5708rad)
  Radius = 1.65
FEATURE [Part::Cylinder] Cylinder014005847  label="Válec760"
  Angle = 360
  AttacherType = Attacher::AttachEngine3D
  Height = 8
  Placement = pos=(3.5,6,0) rot=(0,0,1;0rad)
  Radius = 0.7
FEATURE [Part::Box] Box242  label="Krychle212"
  AttacherType = Attacher::AttachEngine3D
  Height = 3.3
  Length = 4
  Placement = pos=(8,56,58.85) rot=(0,0,1;0rad)
  Width = 8
FEATURE [Part::Cylinder] Cylinder014005848  label="Válec761"
  Angle = 360
  AttacherType = Attacher::AttachEngine3D
  Height = 10
  Placement = pos=(8,64,60.5) rot=(1,0,0;1.5708rad)
  Radius = 1.65
FEATURE [Part::Box] Box243  label="Krychle213"
  AttacherType = Attacher::AttachEngine3D
  Height = 3.3
  Length = 4
  Placement = pos=(39,56,27.85) rot=(0,0,1;0rad)
  Width = 8
FEATURE [Part::Cylinder] Cylinder014005849  label="Válec762"
  Angle = 360
  AttacherType = Attacher::AttachEngine3D
  Height = 20
  Placement = pos=(23.5,64,45) rot=(1,0,0;1.5708rad)
  Radius = 12.5
FEATURE [Part::Cylinder] Cylinder014005850  label="Válec763"
  Angle = 360
  AttacherType = Attacher::AttachEngine3D
  Height = 10
  Placement = pos=(39,64,29.5) rot=(1,0,0;1.5708rad)
  Radius = 1.65
FEATURE [Part::Box] Box244  label="Krychle214"
  AttacherType = Attacher::AttachEngine3D
  Height = 3.3
  Length = 4
  Placement = pos=(8,56,27.85) rot=(0,0,1;0rad)
  Width = 8
FEATURE [Part::Cylinder] Cylinder014005851  label="Válec764"
  Angle = 360
  AttacherType = Attacher::AttachEngine3D
  Height = 70
  Placement = pos=(-5,20,16.5) rot=(0,1,0;1.5708rad)
  Radius = 1
FEATURE [Part::Cylinder] Cylinder014005852  label="Válec765"
  Angle = 360
  AttacherType = Attacher::AttachEngine3D
  Height = 10
  Placement = pos=(39,64,60.5) rot=(1,0,0;1.5708rad)
  Radius = 1.65
FEATURE [Part::Box] Box245  label="Krychle215"
  AttacherType = Attacher::AttachEngine3D
  Height = 25
  Length = 4
  Placement = pos=(23.5,56,32.5) rot=(0,0,1;0rad)
  Width = 8
FEATURE [Part::Cylinder] Cylinder014005853  label="Válec766"
  Angle = 360
  AttacherType = Attacher::AttachEngine3D
  Height = 8
  Placement = pos=(53.5,21.25,0) rot=(0,0,1;0rad)
  Radius = 0.75
FEATURE [Part::Cylinder] Cylinder014005854  label="Válec767"
  Angle = 360
  AttacherType = Attacher::AttachEngine3D
  Height = 10
  Placement = pos=(39,64,60.5) rot=(1,0,0;1.5708rad)
  Radius = 1.65
FEATURE [Part::MultiFuse] Fusion001089102
  Placement = pos=(4,0,0) rot=(0,0,1;0rad)
  Shapes = -> [Cylinder014005846,Cylinder014005842,Cylinder014005854,Cylinder014005843,Cylinder014005850]
FEATURE [Part::Box] Box246  label="Krychle216"
  AttacherType = Attacher::AttachEngine3D
  Height = 26
  Length = 58
  Placement = pos=(-0.5,0,-3) rot=(0,0,1;0rad)
  Width = 29
FEATURE [Part::Cylinder] Cylinder014005855  label="Válec768"
  Angle = 360
  AttacherType = Attacher::AttachEngine3D
  Height = 6.5
  Placement = pos=(3.5,6,0) rot=(0,0,1;0rad)
  Radius = 3.5
FEATURE [Part::Box] Box247  label="Krychle217"
  AttacherType = Attacher::AttachEngine3D
  Height = 28
  Length = 62
  Placement = pos=(-2.5,-2,-5) rot=(0,0,1;0rad)
  Width = 31
FEATURE [Part::Cut] Cut005023015002016  label="Základ004"
  Base = -> Box247
  Tool = -> Box246
FEATURE [Part::Box] Box248  label="Krychle218"
  AttacherType = Attacher::AttachEngine3D
  Height = 8
  Length = 26
  Placement = pos=(22.5,22.5,13.5) rot=(0,0,1;0rad)
  Width = 20
FEATURE [Part::Cylinder] Cylinder014005856  label="Válec769"
  Angle = 360
  AttacherType = Attacher::AttachEngine3D
  Height = 6.5
  Placement = pos=(53.5,6,0) rot=(0,0,1;0rad)
  Radius = 3.5
FEATURE [Part::Box] Box249  label="Krychle219"
  AttacherType = Attacher::AttachEngine3D
  Height = 8
  Length = 24
  Placement = pos=(-1.5,12.5,13.5) rot=(0,0,1;0rad)
  Width = 40
FEATURE [Part::Cylinder] Cylinder014005857  label="Válec770"
  Angle = 360
  AttacherType = Attacher::AttachEngine3D
  Height = 8
  Placement = pos=(3.5,21.25,0) rot=(0,0,1;0rad)
  Radius = 0.75
FEATURE [Part::Cylinder] Cylinder014005858  label="Válec771"
  Angle = 360
  AttacherType = Attacher::AttachEngine3D
  Height = 70
  Placement = pos=(-5,6,16.5) rot=(0,1,0;1.5708rad)
  Radius = 1
FEATURE [Part::MultiFuse] Fusion001089104  label="Horni diry013"
  Placement = pos=(0,0,3) rot=(0,0,1;0rad)
  Shapes = -> [Cylinder014005851,Cylinder014005858]
FEATURE [Part::Box] Box250  label="RJ058"
  AttacherType = Attacher::AttachEngine3D
  Height = 13
  Length = 16
  Placement = pos=(32,-5,4.5) rot=(0,0,1;0rad)
  Width = 18.5
FEATURE [Part::Cylinder] Cylinder014005859  label="Válec772"
  Angle = 360
  AttacherType = Attacher::AttachEngine3D
  Height = 6.5
  Placement = pos=(3.5,21.25,0) rot=(0,0,1;0rad)
  Radius = 3.5
FEATURE [Part::MultiFuse] Fusion001089108  label="sloupky007"
  Placement = pos=(0,0,-3.5) rot=(0,0,1;0rad)
  Shapes = -> [Cylinder014005859,Cylinder014005855,Cylinder014005841,Cylinder014005856]
FEATURE [Part::MultiFuse] Fusion001089107  label="bez der004"
  Shapes = -> [Cut005023015002016,Fusion001089108]
FEATURE [Part::Box] Box251  label="Krychle220"
  AttacherType = Attacher::AttachEngine3D
  Height = 5
  Length = 62
  Placement = pos=(-2.5,-15,20.5) rot=(0,0,1;0rad)
  Width = 92
FEATURE [Part::Cylinder] Cylinder014005860  label="Válec773"
  Angle = 360
  AttacherType = Attacher::AttachEngine3D
  Height = 8
  Placement = pos=(53.5,6,0) rot=(0,0,1;0rad)
  Radius = 0.75
FEATURE [Part::MultiFuse] Fusion001089106  label="diry021"
  Placement = pos=(0,0,-4) rot=(0,0,1;0rad)
  Shapes = -> [Cylinder014005857,Cylinder014005847,Cylinder014005853,Cylinder014005860]
FEATURE [Part::Cylinder] Cylinder014005861  label="Válec774"
  Angle = 360
  AttacherType = Attacher::AttachEngine3D
  Height = 5
  Placement = pos=(14.25,1,9.5) rot=(1,0,0;1.5708rad)
  Radius = 0.01
FEATURE [Part::MultiFuse] Fusion001089100  label="RJ a LED004"
  Shapes = -> [Box250,Cylinder014005861]
FEATURE [Part::MultiFuse] Fusion001089111
  Shapes = -> [Fusion001089106,Fusion001089100,Fusion001089104]
FEATURE [Part::Cut] Cut005023015002017
  Base = -> Fusion001089107
  Tool = -> Fusion001089111
FEATURE [Part::Cut] Cut005023015002013  label="PCB002"
  Base = -> Cut005023015002017
  Placement = pos=(0,-13,26) rot=(1,0,0;0rad)
  Tool = -> Fusion001089103
FEATURE [Part::Box] Box252  label="Krychle221"
  AttacherType = Attacher::AttachEngine3D
  Height = 3.3
  Length = 10
  Placement = pos=(52,31,14.85) rot=(0,0,1;0rad)
  Width = 6
FEATURE [Part::Cylinder] Cylinder014005862  label="Válec775"
  Angle = 360
  AttacherType = Attacher::AttachEngine3D
  Height = 10
  Placement = pos=(52,37,16.5) rot=(0,1,0;1.5708rad)
  Radius = 1.65
FEATURE [Part::Box] Box253  label="Krychle222"
  AttacherType = Attacher::AttachEngine3D
  Height = 8
  Length = 6
  Placement = pos=(53.5,22.5,13.5) rot=(0,0,1;0rad)
  Width = 20
FEATURE [Part::MultiFuse] Fusion001089109  label="spodek002"
  Shapes = -> [Box251,Box253,Box249,Box248]
FEATURE [Part::Cylinder] Cylinder014005863  label="Válec776"
  Angle = 360
  AttacherType = Attacher::AttachEngine3D
  Height = 10
  Placement = pos=(52,31,16.5) rot=(0,1,0;1.5708rad)
  Radius = 1.65
FEATURE [Part::FeaturePython] Screw016  label="M6x12-Screw003"  # Fasteners workbench fastener (typed FeaturePython)
  Placement = pos=(6.5,32.5,21.5) rot=(1,0,0;0rad)
  diameter = 8
  invert = false
  length = 0
  matchOuter = false
  offset = 0
  thread = false
  type = 14
FEATURE [Part::MultiFuse] Fusion001089101  label="Diryspodek001"
  Shapes = -> [Box252,Cylinder014005863,Cylinder014005862,Screw014,Screw016]
FEATURE [Part::Cut] Cut005023015002014  label="Spodek001"
  Base = -> Fusion001089109
  Placement = pos=(0,0,-2) rot=(0,0,1;0rad)
  Tool = -> Fusion001089101
FEATURE [Part::Box] Box254  label="Krychle223"
  AttacherType = Attacher::AttachEngine3D
  Height = 43
  Length = 2.5
  Placement = pos=(-2.5,16,23) rot=(0,0,1;0rad)
  Width = 47
FEATURE [Part::MultiFuse] Fusion001089112  label="Main002"
  Placement = pos=(0,0,0.5) rot=(0,0,1;0rad)
  Shapes = -> [Box237,Box241,Box254]
FEATURE [Part::Cylinder] Cylinder014005864  label="Válec777"
  Angle = 360
  AttacherType = Attacher::AttachEngine3D
  Height = 3
  Placement = pos=(12,63,29.5) rot=(1,0,0;1.5708rad)
  Radius = 3.2
FEATURE [Part::Cylinder] Cylinder014005865  label="Válec778"
  Angle = 360
  AttacherType = Attacher::AttachEngine3D
  Height = 3
  Placement = pos=(8,63,29.5) rot=(1,0,0;1.5708rad)
  Radius = 3.2
FEATURE [Part::Box] Box255  label="Krychle224"
  AttacherType = Attacher::AttachEngine3D
  Height = 6.4
  Length = 4
  Placement = pos=(8,60,26.3) rot=(0,0,1;0rad)
  Width = 3
FEATURE [Part::MultiFuse] Fusion001089113  label="Imbus"
  Shapes = -> [Cylinder014005864,Cylinder014005865,Box255]
FEATURE [Part::Feature] Fusion001089113001  label="Imbus001"
  Placement = pos=(31,0,0) rot=(0,0,1;0rad)
  shape: bbox 10.4 x 3 x 6.4 mm, 6 faces (baked)
FEATURE [Part::Feature] Fusion001089113002  label="Imbus002"
  Placement = pos=(31,0,31) rot=(0,0,1;0rad)
  shape: bbox 10.4 x 3 x 6.4 mm, 6 faces (baked)
FEATURE [Part::Feature] Fusion001089113003  label="Imbus003"
  Placement = pos=(0,0,31) rot=(0,0,1;0rad)
  shape: bbox 10.4 x 3 x 6.4 mm, 6 faces (baked)
FEATURE [Part::MultiFuse] Fusion001089105  label="diry020"
  Placement = pos=(0,0,0.5) rot=(0,0,1;0rad)
  Shapes = -> [Cylinder014005844,Cylinder014005849,Cylinder014005848,Cylinder014005845,Cylinder014005852,Screw015,Fusion001089102,Box245,Box244,Box238,Box243,Box242,Box239,Box240,Fusion001089113,Fusion001089113001,Fusion001089113002,Fusion001089113003]
FEATURE [Part::Cut] Cut005023015002015  label="RA002"
  Base = -> Fusion001089112
  Tool = -> Fusion001089105
FEATURE [Part::MultiFuse] Fusion001089110  label="Raxxx"
  Shapes = -> [Cut005023015002013,Cut005023015002014,Cut005023015002015]
FEATURE [Part::Fillet] Fillet004005003  label="RA FinV2"
  Base = -> Fusion001089110
  Edges = 12 edges: [Edge1 r=1,Edge5 r=1,Edge8 r=1,Edge13 r=1,Edge16 r=2,Edge21 r=1,Edge58 r=1,Edge59 r=1,Edge78 r=1,Edge79 r=2,Edge221 r=2,Edge229 r=2]
FEATURE [Part::Feature] Fusion001089113007  label="Motor-with-connector-final003"
  Placement = pos=(23.5,16,45) rot=(-1,0,0;1.5708rad)
  shape: bbox 48 x 60.1 x 42.3 mm, 110 faces (baked)
FEATURE [Part::Box] Box258  label="Krychle227"
  AttacherType = Attacher::AttachEngine3D
  Height = 70
  Length = 73
  Width = 19
FEATURE [Part::Cut] Cut005023015002020  label="Motor"
  Base = -> Fusion001089113007
  Placement = pos=(0,-3,0) rot=(0,0,1;0rad)
  Tool = -> Box258
FEATURE [App::Part] Part001
  Group = -> [support_nema17_EQ5_A_D__v1_1,support_nema17_EQ5_Dec_v1_1,holderDEC,holderRA,Box258,Fusion001089113007,Cut005023015002020]
  Origin = -> Origin001
FEATURE [Part::Feature] Cut005023015002020001  label="Motor001"
  shape: bbox 48 x 57.1 x 42.3 mm, 100 faces (baked)
FEATURE [Part::FeaturePython] Screw018  label="M6x12-Screw004"  # Fasteners workbench fastener (typed FeaturePython)
  Placement = pos=(8.5,34,20.5) rot=(1,0,0;0rad)
  diameter = 8
  invert = false
  length = 0
  matchOuter = false
  offset = 0
  thread = false
  type = 14
FEATURE [Part::Part2DObjectPython] ShapeString022  # Draft 2D object (typed FeaturePython)
  FontFile = <path>
  Placement = pos=(15.3452,-2,30.5072) rot=(1,0,0;1.5708rad)
  Size = 4
  String = DEC
  Tracking = 0
FEATURE [Part::Part2DObjectPython] ShapeString023  # Draft 2D object (typed FeaturePython)
  FontFile = <path>
  Placement = pos=(15.3452,-2,30.5072) rot=(1,0,0;1.5708rad)
  Size = 0.01
  String = .
  Tracking = 0
FEATURE [Part::Extrusion] Extrude092  label="Text TR005"
  Base = -> ShapeString023
  Dir = (0,-1,0)
  DirMode = 2
  FaceMakerClass = Part::FaceMakerBullseye
  LengthFwd = 1
  LengthRev = 0
  Placement = pos=(-6.75,0.5,-33) rot=(0,0,1;0rad)
  Solid = false
  Symmetric = false
FEATURE [Part::Extrusion] Extrude093  label="Text RA005"
  Base = -> ShapeString022
  Dir = (0,-1,0)
  DirMode = 2
  FaceMakerClass = Part::FaceMakerBullseye
  LengthFwd = 1
  LengthRev = 0
  Placement = pos=(40,1,43.5) rot=(0,1,0;3.14159rad)
  Solid = false
  Symmetric = false
FEATURE [Part::Cylinder] Cylinder014005873  label="Válec786"
  Angle = 360
  AttacherType = Attacher::AttachEngine3D
  Height = 6.5
  Placement = pos=(53.5,21.25,0) rot=(0,0,1;0rad)
  Radius = 3.5
FEATURE [Part::Cylinder] Cylinder014005874  label="Válec787"
  Angle = 360
  AttacherType = Attacher::AttachEngine3D
  Height = 8
  Placement = pos=(3.5,21.25,0) rot=(0,0,1;0rad)
  Radius = 0.75
FEATURE [Part::Cylinder] Cylinder014005876  label="Válec789"
  Angle = 360
  AttacherType = Attacher::AttachEngine3D
  Height = 70
  Placement = pos=(-5,20,16.5) rot=(0,1,0;1.5708rad)
  Radius = 1
FEATURE [Part::Box] Box263  label="Krychle232"
  AttacherType = Attacher::AttachEngine3D
  Height = 9
  Length = 26
  Placement = pos=(-2,24,13) rot=(0,0,1;0rad)
  Width = 20
FEATURE [Part::Cylinder] Cylinder014005877  label="Válec790"
  Angle = 360
  AttacherType = Attacher::AttachEngine3D
  Height = 8
  Placement = pos=(53.5,21.25,0) rot=(0,0,1;0rad)
  Radius = 0.75
FEATURE [Part::Box] Box264  label="RJ059"
  AttacherType = Attacher::AttachEngine3D
  Height = 13
  Length = 16
  Placement = pos=(32,-5,4.5) rot=(0,0,1;0rad)
  Width = 18.5
FEATURE [Part::Cylinder] Cylinder014005878  label="Válec791"
  Angle = 360
  AttacherType = Attacher::AttachEngine3D
  Height = 8
  Placement = pos=(3.5,6,0) rot=(0,0,1;0rad)
  Radius = 0.7
FEATURE [Part::Cylinder] Cylinder014005879  label="Válec792"
  Angle = 360
  AttacherType = Attacher::AttachEngine3D
  Height = 6.5
  Placement = pos=(3.5,21.25,0) rot=(0,0,1;0rad)
  Radius = 3.5
FEATURE [Part::Cylinder] Cylinder014005881  label="Válec794"
  Angle = 360
  AttacherType = Attacher::AttachEngine3D
  Height = 8
  Placement = pos=(53.5,6,0) rot=(0,0,1;0rad)
  Radius = 0.75
FEATURE [Part::Box] Box269  label="Krychle237"
  AttacherType = Attacher::AttachEngine3D
  Height = 26
  Length = 58
  Placement = pos=(-0.5,0,-3) rot=(0,0,1;0rad)
  Width = 29
FEATURE [Part::Cylinder] Cylinder014005882  label="Válec795"
  Angle = 360
  AttacherType = Attacher::AttachEngine3D
  Height = 70
  Placement = pos=(-5,6,16.5) rot=(0,1,0;1.5708rad)
  Radius = 1
FEATURE [Part::Box] Box271  label="Krychle238"
  AttacherType = Attacher::AttachEngine3D
  Height = 28
  Length = 62
  Placement = pos=(-2.5,-2,-5) rot=(0,0,1;0rad)
  Width = 31
FEATURE [Part::Cut] Cut005023015002020006  label="Základ005"
  Base = -> Box271
  Tool = -> Box269
FEATURE [Part::Cylinder] Cylinder014005884  label="Válec797"
  Angle = 360
  AttacherType = Attacher::AttachEngine3D
  Height = 6.5
  Placement = pos=(3.5,6,0) rot=(0,0,1;0rad)
  Radius = 3.5
FEATURE [Part::Box] Box272  label="Krychle239"
  AttacherType = Attacher::AttachEngine3D
  Height = 5
  Length = 62
  Placement = pos=(-2.5,-15,20.5) rot=(0,0,1;0rad)
  Width = 78
FEATURE [Part::MultiFuse] Fusion001089113009  label="spodek003"
  Shapes = -> [Box272,Box263]
FEATURE [Part::MultiFuse] Fusion001089113012  label="diry022"
  Placement = pos=(0,0,-4) rot=(0,0,1;0rad)
  Shapes = -> [Cylinder014005874,Cylinder014005878,Cylinder014005877,Cylinder014005881]
FEATURE [Part::MultiFuse] Fusion001089113015  label="Horni diry014"
  Placement = pos=(0,0,3) rot=(0,0,1;0rad)
  Shapes = -> [Cylinder014005876,Cylinder014005882]
FEATURE [Part::MultiFuse] Fusion001089113018
  Shapes = -> [Extrude092,Extrude093]
FEATURE [Part::Cylinder] Cylinder014005885  label="Válec798"
  Angle = 360
  AttacherType = Attacher::AttachEngine3D
  Height = 5
  Placement = pos=(14.25,1,9.5) rot=(1,0,0;1.5708rad)
  Radius = 0.01
FEATURE [Part::MultiFuse] Fusion001089113016  label="RJ a LED005"
  Shapes = -> [Box264,Cylinder014005885]
FEATURE [Part::MultiFuse] Fusion001089113017
  Shapes = -> [Fusion001089113012,Fusion001089113016,Fusion001089113015]
FEATURE [Part::Cylinder] Cylinder014005886  label="Válec799"
  Angle = 360
  AttacherType = Attacher::AttachEngine3D
  Height = 6.5
  Placement = pos=(53.5,6,0) rot=(0,0,1;0rad)
  Radius = 3.5
FEATURE [Part::MultiFuse] Fusion001089113014  label="sloupky008"
  Placement = pos=(0,0,-3.5) rot=(0,0,1;0rad)
  Shapes = -> [Cylinder014005879,Cylinder014005884,Cylinder014005873,Cylinder014005886]
FEATURE [Part::MultiFuse] Fusion001089113010  label="bez der005"
  Shapes = -> [Cut005023015002020006,Fusion001089113014]
FEATURE [Part::Cut] Cut005023015002020004
  Base = -> Fusion001089113010
  Tool = -> Fusion001089113017
FEATURE [Part::Cut] Cut005023015002020003  label="PCB003"
  Base = -> Cut005023015002020004
  Placement = pos=(0,-13,26) rot=(1,0,0;0rad)
  Tool = -> Fusion001089113018
FEATURE [Part::FeaturePython] Screw019  label="M4x25-Screw006"  # Fasteners workbench fastener (typed FeaturePython)
  Placement = pos=(47.5,49,45) rot=(0,-1,0;1.5708rad)
  diameter = 6
  invert = false
  length = 0
  matchOuter = false
  offset = 0
  thread = false
  type = 13
FEATURE [Part::Feature] Fusion001089113020  label="Imbus004"
  Placement = pos=(0,0,31) rot=(0,0,1;0rad)
  shape: bbox 10.4 x 3 x 6.4 mm, 6 faces (baked)
FEATURE [Part::Feature] Fusion001089113021  label="Imbus005"
  Placement = pos=(31,0,31) rot=(0,0,1;0rad)
  shape: bbox 10.4 x 3 x 6.4 mm, 6 faces (baked)
FEATURE [Part::Feature] Fusion001089113022  label="Imbus006"
  Placement = pos=(31,0,0) rot=(0,0,1;0rad)
  shape: bbox 10.4 x 3 x 6.4 mm, 6 faces (baked)
FEATURE [Part::Box] Box273  label="Krychle240"
  AttacherType = Attacher::AttachEngine3D
  Height = 43
  Length = 65
  Placement = pos=(-5,15.5,49.5) rot=(1,0,0;0.523599rad)
  Width = 48
FEATURE [Part::Cylinder] Cylinder014005887  label="Válec800"
  Angle = 360
  AttacherType = Attacher::AttachEngine3D
  Height = 10
  Placement = pos=(8,64,29.5) rot=(1,0,0;1.5708rad)
  Radius = 1.65
FEATURE [Part::Box] Box274  label="konektor004"
  AttacherType = Attacher::AttachEngine3D
  Height = 29
  Length = 10
  Placement = pos=(50,16,37) rot=(0,0,1;0rad)
  Width = 12
FEATURE [Part::Box] Box275  label="Krychle241"
  AttacherType = Attacher::AttachEngine3D
  Height = 43
  Length = 4
  Placement = pos=(55.5,16,23) rot=(0,0,1;0rad)
  Width = 40
FEATURE [Part::Box] Box276  label="Krychle242"
  AttacherType = Attacher::AttachEngine3D
  Height = 25
  Length = 4
  Placement = pos=(23.5,56,32.5) rot=(0,0,1;0rad)
  Width = 8
FEATURE [Part::Box] Box277  label="Krychle243"
  AttacherType = Attacher::AttachEngine3D
  Height = 3.3
  Length = 4
  Placement = pos=(8,56,27.85) rot=(0,0,1;0rad)
  Width = 8
FEATURE [Part::Cylinder] Cylinder014005888  label="Válec801"
  Angle = 360
  AttacherType = Attacher::AttachEngine3D
  Height = 10
  Placement = pos=(39,64,60.5) rot=(1,0,0;1.5708rad)
  Radius = 1.65
FEATURE [Part::Box] Box278  label="Krychle244"
  AttacherType = Attacher::AttachEngine3D
  Height = 43
  Length = 59.5
  Placement = pos=(0,56,23) rot=(0,0,1;0rad)
  Width = 7
FEATURE [Part::Cylinder] Cylinder014005889  label="Válec802"
  Angle = 360
  AttacherType = Attacher::AttachEngine3D
  Height = 10
  Placement = pos=(8,64,60.5) rot=(1,0,0;1.5708rad)
  Radius = 1.65
FEATURE [Part::Cylinder] Cylinder014005890  label="Válec803"
  Angle = 360
  AttacherType = Attacher::AttachEngine3D
  Height = 20
  Placement = pos=(23.5,64,45) rot=(1,0,0;1.5708rad)
  Radius = 12.5
FEATURE [Part::Cylinder] Cylinder014005891  label="Válec804"
  Angle = 360
  AttacherType = Attacher::AttachEngine3D
  Height = 10
  Placement = pos=(8,64,60.5) rot=(1,0,0;1.5708rad)
  Radius = 1.65
FEATURE [Part::Box] Box279  label="Krychle245"
  AttacherType = Attacher::AttachEngine3D
  Height = 3.3
  Length = 4
  Placement = pos=(8,56,58.85) rot=(0,0,1;0rad)
  Width = 8
FEATURE [Part::Box] Box280  label="Krychle246"
  AttacherType = Attacher::AttachEngine3D
  Height = 3.3
  Length = 4
  Placement = pos=(39,56,27.85) rot=(0,0,1;0rad)
  Width = 8
FEATURE [Part::Cylinder] Cylinder014005892  label="Válec805"
  Angle = 360
  AttacherType = Attacher::AttachEngine3D
  Height = 10
  Placement = pos=(39,64,29.5) rot=(1,0,0;1.5708rad)
  Radius = 1.65
FEATURE [Part::Cylinder] Cylinder014005893  label="Válec806"
  Angle = 360
  AttacherType = Attacher::AttachEngine3D
  Height = 10
  Placement = pos=(39,64,29.5) rot=(1,0,0;1.5708rad)
  Radius = 1.65
FEATURE [Part::Cylinder] Cylinder014005894  label="Válec807"
  Angle = 360
  AttacherType = Attacher::AttachEngine3D
  Height = 10
  Placement = pos=(8,64,29.5) rot=(1,0,0;1.5708rad)
  Radius = 1.65
FEATURE [Part::Cylinder] Cylinder014005895  label="Válec808"
  Angle = 360
  AttacherType = Attacher::AttachEngine3D
  Height = 20
  Placement = pos=(23.5,64,45) rot=(1,0,0;1.5708rad)
  Radius = 12.5
FEATURE [Part::Box] Box281  label="Krychle247"
  AttacherType = Attacher::AttachEngine3D
  Height = 3.3
  Length = 4
  Placement = pos=(39,56,58.85) rot=(0,0,1;0rad)
  Width = 8
FEATURE [Part::Cylinder] Cylinder014005896  label="Válec809"
  Angle = 360
  AttacherType = Attacher::AttachEngine3D
  Height = 10
  Placement = pos=(39,64,60.5) rot=(1,0,0;1.5708rad)
  Radius = 1.65
FEATURE [Part::MultiFuse] Fusion001089113023
  Placement = pos=(4,0,0) rot=(0,0,1;0rad)
  Shapes = -> [Cylinder014005894,Cylinder014005889,Cylinder014005896,Cylinder014005890,Cylinder014005893]
FEATURE [Part::Cylinder] Cylinder014005897  label="Válec810"
  Angle = 360
  AttacherType = Attacher::AttachEngine3D
  Height = 3
  Placement = pos=(8,63,29.5) rot=(1,0,0;1.5708rad)
  Radius = 3.2
FEATURE [Part::Box] Box282  label="Krychle248"
  AttacherType = Attacher::AttachEngine3D
  Height = 6.4
  Length = 4
  Placement = pos=(8,60,26.3) rot=(0,0,1;0rad)
  Width = 3
FEATURE [Part::Box] Box283  label="Krychle249"
  AttacherType = Attacher::AttachEngine3D
  Height = 43
  Length = 2.5
  Placement = pos=(-2.5,16,23) rot=(0,0,1;0rad)
  Width = 47
FEATURE [Part::MultiFuse] Fusion001089113025  label="Main004"
  Placement = pos=(0,0,0.5) rot=(0,0,1;0rad)
  Shapes = -> [Box278,Box275,Box283]
FEATURE [Part::Cylinder] Cylinder014005898  label="Válec811"
  Angle = 360
  AttacherType = Attacher::AttachEngine3D
  Height = 3
  Placement = pos=(12,63,29.5) rot=(1,0,0;1.5708rad)
  Radius = 3.2
FEATURE [Part::MultiFuse] Fusion001089113026  label="Imbus007"
  Shapes = -> [Cylinder014005898,Cylinder014005897,Box282]
FEATURE [Part::MultiFuse] Fusion001089113024  label="diry024"
  Placement = pos=(0,0,0.5) rot=(0,0,1;0rad)
  Shapes = -> [Cylinder014005887,Cylinder014005895,Cylinder014005891,Cylinder014005892,Cylinder014005888,Screw019,Fusion001089113023,Box276,Box277,Box281,Box280,Box279,Box274,Box273,Fusion001089113026,Fusion001089113022,Fusion001089113021,Fusion001089113020]
FEATURE [Part::Cut] Cut005023015002020007  label="DE003"
  Base = -> Fusion001089113025
  Tool = -> Fusion001089113024
FEATURE [Part::FeaturePython] Screw020  label="M6x12-Screw005"  # Fasteners workbench fastener (typed FeaturePython)
  Placement = pos=(8.5,34,21.5) rot=(1,0,0;0rad)
  diameter = 8
  invert = false
  length = 0
  matchOuter = false
  offset = 0
  thread = false
  type = 14
FEATURE [Part::MultiFuse] Fusion001089113027
  Shapes = -> [Screw020,Screw018]
FEATURE [Part::Cut] Cut005023015002020008
  Base = -> Fusion001089113009
  Placement = pos=(0,0,-2) rot=(0,0,1;0rad)
  Tool = -> Fusion001089113027
FEATURE [Part::MultiFuse] Fusion001089113028  label="DECV2"
  Shapes = -> [Cut005023015002020003,Cut005023015002020007,Cut005023015002020008]
FEATURE [Part::Fillet] Fillet004005003002  label="DEv2"
  Base = -> Fusion001089113028
  Edges = 13 edges r=1: [Edge9,Edge48,Edge101,Edge104,Edge181,Edge273,Edge274,Edge375,Edge376,Edge388,Edge389,Edge391,Edge396]
FEATURE [Part::Feature] Fillet004005003002001  label="DEv003"
  shape: bbox 62 x 78 x 55.5 mm, 180 faces (baked)
FEATURE [Part::Feature] Cut005023015002020009  label="Jezdec001"
  shape: bbox 49 x 12 x 43 mm, 24 faces (baked)
FEATURE [Part::FeaturePython] Screw021  label="M4x25-Screw007"  # Fasteners workbench fastener (typed FeaturePython)
  Placement = pos=(47.5,49,45) rot=(0,-1,0;1.5708rad)
  diameter = 6
  invert = false
  length = 0
  matchOuter = false
  offset = 0
  thread = false
  type = 13
FEATURE [Part::Feature] Fillet004005003002002  label="RA FinV003"
  shape: bbox 62 x 92 x 55 mm, 179 faces (baked)
FEATURE [Part::Part2DObjectPython] ShapeString004  # Draft 2D object (typed FeaturePython)
  FontFile = <path>
  Placement = pos=(15.3452,-2,30.5072) rot=(1,0,0;1.5708rad)
  Size = 10
  String = OnStep
  Tracking = 0
FEATURE [Part::Box] Box022  label="Krychle011"
  AttacherType = Attacher::AttachEngine3D
  Height = 2
  Length = 62
  Placement = pos=(-2.5,-2,23) rot=(0,0,1;0rad)
  Width = 26
FEATURE [Part::Box] Box023  label="Krychle012"
  AttacherType = Attacher::AttachEngine3D
  Height = 8
  Length = 58
  Placement = pos=(-0.5,0,15) rot=(0,0,1;0rad)
  Width = 23
FEATURE [Part::MultiFuse] Fusion029
  Shapes = -> [Box022,Box023]
FEATURE [Part::Box] Box024  label="Krychle013"
  AttacherType = Attacher::AttachEngine3D
  Height = 8
  Length = 54
  Placement = pos=(1.5,0,15) rot=(0,0,1;0rad)
  Width = 29
FEATURE [Part::Cylinder] Cylinder040  label="Válec039"
  Angle = 360
  AttacherType = Attacher::AttachEngine3D
  Height = 70
  Placement = pos=(-5,20,16.5) rot=(0,1,0;1.5708rad)
  Radius = 1
FEATURE [Part::Cylinder] Cylinder039  label="Válec038"
  Angle = 360
  AttacherType = Attacher::AttachEngine3D
  Height = 70
  Placement = pos=(-5,6,16.5) rot=(0,1,0;1.5708rad)
  Radius = 1
FEATURE [Part::MultiFuse] Fusion028  label="Horni diry002"
  Placement = pos=(0,0,3) rot=(0,0,1;0rad)
  Shapes = -> [Cylinder040,Cylinder039]
FEATURE [Part::MultiFuse] Fusion030
  Shapes = -> [Fusion028,Box024]
FEATURE [Part::Cut] Cut018
  Base = -> Fusion029
  Tool = -> Fusion030
FEATURE [Part::Extrusion] Extrude004  label="OnStep"
  Base = -> ShapeString004
  Dir = (0,-1,0)
  DirMode = 2
  FaceMakerClass = Part::FaceMakerBullseye
  LengthFwd = 1
  LengthRev = 0
  Placement = pos=(-10,-22,22) rot=(-1,0,0;1.5708rad)
  Solid = false
  Symmetric = false
FEATURE [Part::Cut] Cut019  label="viko s texty"
  Base = -> Cut018
  Tool = -> Extrude004
FEATURE [Part::Chamfer] Chamfer  label="Vyko "
  Base = -> Cut019
  Edges = 2 edges r=3: [Edge353,Edge357]
FEATURE [Part::FeaturePython] Screw009  label="M4x30-Screw003"  # Fasteners workbench fastener (typed FeaturePython)
  Placement = pos=(0,0,2.25) rot=(0,0,1;0rad)
  diameter = 6
  invert = false
  length = 1
  matchOuter = false
  offset = 0
  thread = false
  type = 13
FEATURE [Part::Feature] Cylinder112024025003003006010004077  label="Válec229"
  Placement = pos=(0,0,0) rot=(0,0,1;0.349066rad)
  shape: bbox 2 x 2 x 10 mm, 3 faces (baked)
FEATURE [Part::Feature] Fusion005043005007002046
  Placement = pos=(0,0,0) rot=(0,0,1;2.0944rad)
  shape: bbox 6.25 x 14.82 x 10 mm, 18 faces, 6 solids (baked)
FEATURE [Part::Feature] Cylinder112024025003003006010004078  label="Válec230"
  Placement = pos=(0,0,0) rot=(0,0,1;0.698132rad)
  shape: bbox 2 x 2 x 10 mm, 3 faces (baked)
FEATURE [Part::Cylinder] Cylinder112024025003003006010004076  label="Válec228"
  Angle = 360
  AttacherType = Attacher::AttachEngine3D
  Height = 5
  Radius = 8.5
FEATURE [Part::Cut] Cut018020020009027020002003004004023
  Base = -> Cylinder112024025003003006010004076
  Tool = -> Screw009
FEATURE [Part::Fillet] Fillet024  label="knob003"
  Base = -> Cut018020020009027020002003004004023
  Edges = 2 edges r=2: [Edge1,Edge3]
FEATURE [Part::Cylinder] Cylinder112024025003003006010004075  label="Válec227"
  Angle = 360
  AttacherType = Attacher::AttachEngine3D
  Height = 10
  Placement = pos=(8.5,0,0) rot=(0,0,1;0.349066rad)
  Radius = 1
FEATURE [Part::MultiFuse] Fusion005043005007002045
  Shapes = -> [Cylinder112024025003003006010004075,Cylinder112024025003003006010004077,Cylinder112024025003003006010004078]
FEATURE [Part::Feature] Fusion005043005007002048
  Placement = pos=(0,0,0) rot=(0,0,1;4.18879rad)
  shape: bbox 14.24 x 7.464 x 10 mm, 18 faces, 6 solids (baked)
FEATURE [Part::Feature] Fusion005043005007002047
  Placement = pos=(0,0,0) rot=(0,0,1;1.0472rad)
  shape: bbox 7.726 x 3.01 x 10 mm, 9 faces, 3 solids (baked)
FEATURE [Part::MultiFuse] Fusion005043005007002044
  Shapes = -> [Fusion005043005007002045,Fusion005043005007002047]
FEATURE [Part::MultiFuse] Fusion005043005007002043
  Shapes = -> [Fusion005043005007002048,Fusion005043005007002046,Fusion005043005007002044]
FEATURE [Part::Cut] Cut018020020009027020002003004004024  label="Knob M4 v003"
  Base = -> Fillet024
  Placement = pos=(60,49,45) rot=(0,1,0;1.5708rad)
  Tool = -> Fusion005043005007002043
FEATURE [Part::Cylinder] Cylinder112024025003003006010004079  label="Válec812"
  Angle = 360
  AttacherType = Attacher::AttachEngine3D
  Height = 22
  Radius = 17.6
FEATURE [Part::Cylinder] Cylinder112024025003003006010004080  label="Válec813"
  Angle = 360
  AttacherType = Attacher::AttachEngine3D
  Height = 14
  Placement = pos=(0,0,8) rot=(0,0,1;0rad)
  Radius = 22
FEATURE [Part::Cylinder] Cylinder112024025003003006010004081  label="Válec814"
  Angle = 360
  AttacherType = Attacher::AttachEngine3D
  Height = 8
  Placement = pos=(0,0,14) rot=(0,0,1;0rad)
  Radius = 17.8
FEATURE [Part::Cylinder] Cylinder112024025003003006010004082  label="Válec815"
  Angle = 360
  AttacherType = Attacher::AttachEngine3D
  Height = 25
  Radius = 16
FEATURE [Part::Cylinder] Cylinder112024025003003006010004083  label="Válec816"
  Angle = 360
  AttacherType = Attacher::AttachEngine3D
  Height = 13
  Placement = pos=(15,0,12) rot=(0,1,0;1.5708rad)
  Radius = 1.8
FEATURE [Part::Box] Box284  label="Krychle250"
  AttacherType = Attacher::AttachEngine3D
  Height = 8
  Length = 10
  Placement = pos=(18,-7,8) rot=(0,0,1;0rad)
  Width = 14
FEATURE [Part::MultiFuse] Fusion005043005007002049  label="telo"
  Shapes = -> [Cylinder112024025003003006010004079,Cylinder112024025003003006010004080,Box284]
FEATURE [Part::Box] Box285  label="Krychle251"
  AttacherType = Attacher::AttachEngine3D
  Height = 8
  Length = 2
  Placement = pos=(-1,-20,0) rot=(0,0,1;0rad)
  Width = 40
FEATURE [Part::Box] Box286  label="Krychle252"
  AttacherType = Attacher::AttachEngine3D
  Height = 8
  Length = 40
  Placement = pos=(-20,-1,0) rot=(0,0,1;0rad)
  Width = 2
FEATURE [Part::Cylinder] Cylinder112024025003003006010004084  label="Válec817"
  Angle = 360
  AttacherType = Attacher::AttachEngine3D
  Height = 11
  Placement = pos=(25,4,12) rot=(0,0,1;0rad)
  Radius = 1
FEATURE [Part::Cylinder] Cylinder112024025003003006010004085  label="Válec818"
  Angle = 360
  AttacherType = Attacher::AttachEngine3D
  Height = 11
  Placement = pos=(25,-4,12) rot=(0,0,1;0rad)
  Radius = 1
FEATURE [Part::Box] Box287  label="Krychle253"
  AttacherType = Attacher::AttachEngine3D
  Height = 4
  Length = 6
  Placement = pos=(22,-7,12) rot=(0,0,1;0rad)
  Width = 14
FEATURE [Part::Box] Box288  label="Krychle254"
  AttacherType = Attacher::AttachEngine3D
  Height = 4
  Length = 6
  Placement = pos=(22,-7,12) rot=(0,0,1;0rad)
  Width = 14
FEATURE [Part::Cylinder] Cylinder112024025003003006010004086  label="Válec819"
  Angle = 360
  AttacherType = Attacher::AttachEngine3D
  Height = 11
  Placement = pos=(25,4,12) rot=(0,0,1;0rad)
  Radius = 1
FEATURE [Part::Cylinder] Cylinder112024025003003006010004087  label="Válec820"
  Angle = 360
  AttacherType = Attacher::AttachEngine3D
  Height = 11
  Placement = pos=(25,-4,12) rot=(0,0,1;0rad)
  Radius = 1
FEATURE [Part::Cylinder] Cylinder112024025003003006010004088  label="Válec821"
  Angle = 360
  AttacherType = Attacher::AttachEngine3D
  Height = 13
  Placement = pos=(15,0,12) rot=(0,1,0;1.5708rad)
  Radius = 1.5
FEATURE [Part::MultiFuse] Fusion005043005007002051
  Shapes = -> [Cylinder112024025003003006010004086,Cylinder112024025003003006010004087,Cylinder112024025003003006010004088]
FEATURE [Part::Cut] Cut018020020009027020002003004004026  label="CableHolder"
  Base = -> Box288
  Tool = -> Fusion005043005007002051
FEATURE [Part::Cylinder] Cylinder112024025003003006010004089  label="Válec822"
  Angle = 360
  AttacherType = Attacher::AttachEngine3D
  Height = 13
  Placement = pos=(9,0,11.5) rot=(0,1,0;1.5708rad)
  Radius = 2.2
FEATURE [Part::MultiFuse] Fusion005043005007002050  label="diry025"
  Shapes = -> [Cylinder112024025003003006010004081,Cylinder112024025003003006010004082,Cylinder112024025003003006010004083,Box285,Box286,Cylinder112024025003003006010004084,Cylinder112024025003003006010004085,Box287,Cylinder112024025003003006010004089]
FEATURE [Part::Cut] Cut018020020009027020002003004004025  label="Polar scope Iluminator"
  Base = -> Fusion005043005007002049
  Tool = -> Fusion005043005007002050
FEATURE [Part::Box] Box289  label="Krychle255"
  AttacherType = Attacher::AttachEngine3D
  Height = 16.5
  Length = 10
  Placement = pos=(-5,1.6,0) rot=(0,0,1;0rad)
  Width = 1.6
FEATURE [Part::Cylinder] Cylinder112024025003003006010004090  label="Válec823"
  Angle = 360
  AttacherType = Attacher::AttachEngine3D
  Height = 13
  Placement = pos=(0,12,5.5) rot=(1,0,0;1.5708rad)
  Radius = 1.5
FEATURE [Part::Feature] difference001002  label="difference003"
  Placement = pos=(0,0,0) rot=(0,0,1;1.0472rad)
  shape: bbox 27.96 x 27.96 x 17.5 mm, 1020 faces (baked)
FEATURE [Part::Cylinder] Cylinder112024025003003006010004091  label="Válec824"
  Angle = 360
  AttacherType = Attacher::AttachEngine3D
  Height = 1.5
  Radius = 5
FEATURE [Part::Cylinder] Cylinder112024025003003006010004092  label="Válec825"
  Angle = 360
  AttacherType = Attacher::AttachEngine3D
  Height = 10
  Radius = 3.3
FEATURE [Part::Cut] Cut018020020009027020002003004004028  label="Ring"
  Base = -> Cylinder112024025003003006010004091
  Tool = -> Cylinder112024025003003006010004092
FEATURE [Part::Cylinder] Cylinder112024025003003006010004093  label="Válec826"
  Angle = 360
  AttacherType = Attacher::AttachEngine3D
  Height = 10
  Radius = 10.5
FEATURE [Part::Cylinder] Cylinder112024025003003006010004094  label="Válec827"
  Angle = 360
  AttacherType = Attacher::AttachEngine3D
  Height = 10
  Radius = 3.2
FEATURE [Part::Cut] Cut018020020009027020002003004004029
  Base = -> Cylinder112024025003003006010004093
  Tool = -> Cylinder112024025003003006010004094
FEATURE [Part::MultiFuse] Fusion005043005007002052
  Shapes = -> [Box289,difference001002,Cut018020020009027020002003004004029]
FEATURE [Part::Cut] Cut018020020009027020002003004004027  label="Pulley40"
  Base = -> Fusion005043005007002052
  Tool = -> Cylinder112024025003003006010004090
FEATURE [App::Part] Part002  label="FinEQ5"
  Group = -> [Cylinder014005808,Box206,Box205,Cylinder014005804,Cylinder014005807,Cylinder014005806,Fusion,Cylinder014005805,Fusion001089078,Screw010,Cut,Fusion001089085,Cut005023015002010,Cut005023015002009,Cut005023015002008,Cut005023015002012,Cut005023015002011,Cylinder014005823,Cylinder014005826,Box224,Cylinder014005828,Cylinder014005829,Cylinder014005821,Box220,Box221,Box226,Cylinder014005820,+293 more]
  Origin = -> Origin002
FEATURE [Part::Feature] Cut018020020009027020002003004004027001  label="Pulley041"
  shape: bbox 27.96 x 27.96 x 17.5 mm, 994 faces (baked)
FEATURE [App::Part] Part003  label="iIluminator"
  Group = -> [Fusion005043005007002050,Fusion005043005007002049,Box285,Cylinder112024025003003006010004085,Cylinder112024025003003006010004079,Cylinder112024025003003006010004082,Cylinder112024025003003006010004080,Cylinder112024025003003006010004081,Cylinder112024025003003006010004083,Box284,Box286,Box287,Cylinder112024025003003006010004089,Cylinder112024025003003006010004084,+8 more]
  Origin = -> Origin003
FEATURE [Part::Part2DObjectPython] ShapeString024  # Draft 2D object (typed FeaturePython)
  FontFile = <path>
  Placement = pos=(15.3452,-2,30.5072) rot=(1,0,0;1.5708rad)
  Size = 0.01
  String = .
  Tracking = 0
FEATURE [Part::Part2DObjectPython] ShapeString025  # Draft 2D object (typed FeaturePython)
  FontFile = <path>
  Placement = pos=(15.3452,-2,30.5072) rot=(1,0,0;1.5708rad)
  Size = 4
  String = DEC
  Tracking = 0
FEATURE [Part::Cylinder] Cylinder112024025003003006010004095  label="Válec828"
  Angle = 360
  AttacherType = Attacher::AttachEngine3D
  Height = 8
  Placement = pos=(53.5,21.25,0) rot=(0,0,1;0rad)
  Radius = 0.75
FEATURE [Part::Cylinder] Cylinder112024025003003006010004096  label="Válec829"
  Angle = 360
  AttacherType = Attacher::AttachEngine3D
  Height = 10
  Placement = pos=(8,64,29.5) rot=(1,0,0;1.5708rad)
  Radius = 1.65
FEATURE [Part::Box] Box290  label="Krychle256"
  AttacherType = Attacher::AttachEngine3D
  Height = 43
  Length = 4
  Placement = pos=(55.5,16,23) rot=(0,0,1;0rad)
  Width = 40
FEATURE [Part::Box] Box291  label="Krychle257"
  AttacherType = Attacher::AttachEngine3D
  Height = 3.3
  Length = 4
  Placement = pos=(8,56,27.85) rot=(0,0,1;0rad)
  Width = 8
FEATURE [Part::Cylinder] Cylinder112024025003003006010004097  label="Válec830"
  Angle = 360
  AttacherType = Attacher::AttachEngine3D
  Height = 5
  Placement = pos=(14.25,1,9.5) rot=(1,0,0;1.5708rad)
  Radius = 0.01
FEATURE [Part::Cylinder] Cylinder112024025003003006010004098  label="Válec831"
  Angle = 360
  AttacherType = Attacher::AttachEngine3D
  Height = 10
  Placement = pos=(8,64,60.5) rot=(1,0,0;1.5708rad)
  Radius = 1.65
FEATURE [Part::Cylinder] Cylinder112024025003003006010004099  label="Válec832"
  Angle = 360
  AttacherType = Attacher::AttachEngine3D
  Height = 10
  Placement = pos=(8,64,60.5) rot=(1,0,0;1.5708rad)
  Radius = 1.65
FEATURE [Part::Box] Box293  label="Krychle259"
  AttacherType = Attacher::AttachEngine3D
  Height = 26
  Length = 58
  Placement = pos=(-0.5,0,-3) rot=(0,0,1;0rad)
  Width = 29
FEATURE [Part::Extrusion] Extrude094  label="Text TR006"
  Base = -> ShapeString024
  Dir = (0,-1,0)
  DirMode = 2
  FaceMakerClass = Part::FaceMakerBullseye
  LengthFwd = 1
  LengthRev = 0
  Placement = pos=(-6.75,0.5,-33) rot=(0,0,1;0rad)
  Solid = false
  Symmetric = false
FEATURE [Part::Extrusion] Extrude095  label="Text RA006"
  Base = -> ShapeString025
  Dir = (0,-1,0)
  DirMode = 2
  FaceMakerClass = Part::FaceMakerBullseye
  LengthFwd = 1
  LengthRev = 0
  Placement = pos=(40,1,43.5) rot=(0,1,0;3.14159rad)
  Solid = false
  Symmetric = false
FEATURE [Part::MultiFuse] Fusion005043005007002066
  Shapes = -> [Extrude094,Extrude095]
FEATURE [Part::Cylinder] Cylinder112024025003003006010004100  label="Válec833"
  Angle = 360
  AttacherType = Attacher::AttachEngine3D
  Height = 8
  Placement = pos=(3.5,21.25,0) rot=(0,0,1;0rad)
  Radius = 0.75
FEATURE [Part::Box] Box294  label="RJ060"
  AttacherType = Attacher::AttachEngine3D
  Height = 13
  Length = 16
  Placement = pos=(32,-5,4.5) rot=(0,0,1;0rad)
  Width = 18.5
FEATURE [Part::MultiFuse] Fusion005043005007002060  label="RJ a LED006"
  Shapes = -> [Box294,Cylinder112024025003003006010004097]
FEATURE [Part::Cylinder] Cylinder112024025003003006010004101  label="Válec834"
  Angle = 360
  AttacherType = Attacher::AttachEngine3D
  Height = 6.5
  Placement = pos=(3.5,21.25,0) rot=(0,0,1;0rad)
  Radius = 3.5
FEATURE [Part::Cylinder] Cylinder112024025003003006010004102  label="Válec835"
  Angle = 360
  AttacherType = Attacher::AttachEngine3D
  Height = 8
  Placement = pos=(53.5,6,0) rot=(0,0,1;0rad)
  Radius = 0.75
FEATURE [Part::Cylinder] Cylinder112024025003003006010004103  label="Válec836"
  Angle = 360
  AttacherType = Attacher::AttachEngine3D
  Height = 6.5
  Placement = pos=(53.5,21.25,0) rot=(0,0,1;0rad)
  Radius = 3.5
FEATURE [Part::Box] Box295  label="Krychle260"
  AttacherType = Attacher::AttachEngine3D
  Height = 28
  Length = 62
  Placement = pos=(-2.5,-2,-5) rot=(0,0,1;0rad)
  Width = 31
FEATURE [Part::Cylinder] Cylinder112024025003003006010004104  label="Válec837"
  Angle = 360
  AttacherType = Attacher::AttachEngine3D
  Height = 6.5
  Placement = pos=(53.5,6,0) rot=(0,0,1;0rad)
  Radius = 3.5
FEATURE [Part::Cylinder] Cylinder112024025003003006010004105  label="Válec838"
  Angle = 360
  AttacherType = Attacher::AttachEngine3D
  Height = 70
  Placement = pos=(-5,20,16.5) rot=(0,1,0;1.5708rad)
  Radius = 1
FEATURE [Part::Cylinder] Cylinder112024025003003006010004106  label="Válec839"
  Angle = 360
  AttacherType = Attacher::AttachEngine3D
  Height = 6.5
  Placement = pos=(3.5,6,0) rot=(0,0,1;0rad)
  Radius = 3.5
FEATURE [Part::MultiFuse] Fusion005043005007002057  label="sloupky009"
  Placement = pos=(0,0,-3.5) rot=(0,0,1;0rad)
  Shapes = -> [Cylinder112024025003003006010004101,Cylinder112024025003003006010004106,Cylinder112024025003003006010004103,Cylinder112024025003003006010004104]
FEATURE [Part::Box] Box296  label="Krychle261"
  AttacherType = Attacher::AttachEngine3D
  Height = 3
  Length = 62
  Placement = pos=(-2.5,-15,20.5) rot=(0,0,1;0rad)
  Width = 78
FEATURE [Part::Cylinder] Cylinder112024025003003006010004107  label="Válec840"
  Angle = 360
  AttacherType = Attacher::AttachEngine3D
  Height = 70
  Placement = pos=(-5,6,16.5) rot=(0,1,0;1.5708rad)
  Radius = 1
FEATURE [Part::MultiFuse] Fusion005043005007002059  label="Horni diry015"
  Placement = pos=(0,0,3) rot=(0,0,1;0rad)
  Shapes = -> [Cylinder112024025003003006010004105,Cylinder112024025003003006010004107]
FEATURE [Part::Cylinder] Cylinder112024025003003006010004108  label="Válec841"
  Angle = 360
  AttacherType = Attacher::AttachEngine3D
  Height = 8
  Placement = pos=(3.5,6,0) rot=(0,0,1;0rad)
  Radius = 0.7
FEATURE [Part::MultiFuse] Fusion005043005007002056  label="diry026"
  Placement = pos=(0,0,-4) rot=(0,0,1;0rad)
  Shapes = -> [Cylinder112024025003003006010004100,Cylinder112024025003003006010004108,Cylinder112024025003003006010004095,Cylinder112024025003003006010004102]
FEATURE [Part::MultiFuse] Fusion005043005007002063
  Shapes = -> [Fusion005043005007002056,Fusion005043005007002060,Fusion005043005007002059]
FEATURE [Part::Box] Box297  label="Krychle262"
  AttacherType = Attacher::AttachEngine3D
  Height = 43
  Length = 66
  Placement = pos=(-6,15.5,49.5) rot=(1,0,0;0.523599rad)
  Width = 48
FEATURE [Part::Box] Box298  label="konektor005"
  AttacherType = Attacher::AttachEngine3D
  Height = 29
  Length = 10
  Placement = pos=(50,16,37) rot=(0,0,1;0rad)
  Width = 12
FEATURE [Part::Box] Box299  label="Krychle263"
  AttacherType = Attacher::AttachEngine3D
  Height = 25
  Length = 4
  Placement = pos=(23.5,56,32.5) rot=(0,0,1;0rad)
  Width = 8
FEATURE [Part::Box] Box300  label="Krychle264"
  AttacherType = Attacher::AttachEngine3D
  Height = 43
  Length = 59.5
  Placement = pos=(0,56,23) rot=(0,0,1;0rad)
  Width = 7
FEATURE [Part::Cylinder] Cylinder112024025003003006010004109  label="Válec842"
  Angle = 360
  AttacherType = Attacher::AttachEngine3D
  Height = 10
  Placement = pos=(39,64,60.5) rot=(1,0,0;1.5708rad)
  Radius = 1.65
FEATURE [Part::Cylinder] Cylinder112024025003003006010004110  label="Válec843"
  Angle = 360
  AttacherType = Attacher::AttachEngine3D
  Height = 20
  Placement = pos=(23.5,64,45) rot=(1,0,0;1.5708rad)
  Radius = 12.5
FEATURE [Part::Box] Box301  label="Krychle265"
  AttacherType = Attacher::AttachEngine3D
  Height = 3.3
  Length = 4
  Placement = pos=(8,56,58.85) rot=(0,0,1;0rad)
  Width = 8
FEATURE [Part::Cylinder] Cylinder112024025003003006010004111  label="Válec844"
  Angle = 360
  AttacherType = Attacher::AttachEngine3D
  Height = 10
  Placement = pos=(8,64,29.5) rot=(1,0,0;1.5708rad)
  Radius = 1.65
FEATURE [Part::Cylinder] Cylinder112024025003003006010004112  label="Válec845"
  Angle = 360
  AttacherType = Attacher::AttachEngine3D
  Height = 20
  Placement = pos=(23.5,64,45) rot=(1,0,0;1.5708rad)
  Radius = 12.5
FEATURE [Part::Cylinder] Cylinder112024025003003006010004113  label="Válec846"
  Angle = 360
  AttacherType = Attacher::AttachEngine3D
  Height = 3
  Placement = pos=(8,63,29.5) rot=(1,0,0;1.5708rad)
  Radius = 3.2
FEATURE [Part::Box] Box302  label="Krychle266"
  AttacherType = Attacher::AttachEngine3D
  Height = 6.4
  Length = 4
  Placement = pos=(8,60,26.3) rot=(0,0,1;0rad)
  Width = 3
FEATURE [Part::Cylinder] Cylinder112024025003003006010004114  label="Válec847"
  Angle = 360
  AttacherType = Attacher::AttachEngine3D
  Height = 10
  Placement = pos=(39,64,29.5) rot=(1,0,0;1.5708rad)
  Radius = 1.65
FEATURE [Part::Box] Box303  label="Krychle267"
  AttacherType = Attacher::AttachEngine3D
  Height = 43
  Length = 6
  Placement = pos=(-6,16,23) rot=(0,0,1;0rad)
  Width = 47
FEATURE [Part::MultiFuse] Fusion005043005007002065  label="Main005"
  Placement = pos=(0,0,0.5) rot=(0,0,1;0rad)
  Shapes = -> [Box300,Box290,Box303]
FEATURE [Part::Cylinder] Cylinder112024025003003006010004115  label="Válec848"
  Angle = 360
  AttacherType = Attacher::AttachEngine3D
  Height = 3
  Placement = pos=(12,63,29.5) rot=(1,0,0;1.5708rad)
  Radius = 3.2
FEATURE [Part::MultiFuse] Fusion005043005007002062  label="Imbus008"
  Shapes = -> [Cylinder112024025003003006010004115,Cylinder112024025003003006010004113,Box302]
FEATURE [Part::Box] Box304  label="Krychle268"
  AttacherType = Attacher::AttachEngine3D
  Height = 3.3
  Length = 4
  Placement = pos=(39,56,58.85) rot=(0,0,1;0rad)
  Width = 8
FEATURE [Part::Cylinder] Cylinder112024025003003006010004116  label="Válec849"
  Angle = 360
  AttacherType = Attacher::AttachEngine3D
  Height = 10
  Placement = pos=(39,64,60.5) rot=(1,0,0;1.5708rad)
  Radius = 1.65
FEATURE [Part::MultiFuse] Fusion005043005007002061
  Placement = pos=(4,0,0) rot=(0,0,1;0rad)
  Shapes = -> [Cylinder112024025003003006010004111,Cylinder112024025003003006010004098,Cylinder112024025003003006010004116,Cylinder112024025003003006010004110,Cylinder112024025003003006010004114]
FEATURE [Part::Box] Box305  label="Krychle269"
  AttacherType = Attacher::AttachEngine3D
  Height = 3.3
  Length = 4
  Placement = pos=(39,56,27.85) rot=(0,0,1;0rad)
  Width = 8
FEATURE [Part::Cylinder] Cylinder112024025003003006010004117  label="Válec850"
  Angle = 360
  AttacherType = Attacher::AttachEngine3D
  Height = 10
  Placement = pos=(39,64,29.5) rot=(1,0,0;1.5708rad)
  Radius = 1.65
FEATURE [Part::Cut] Cut018020020009027020002003004004027004  label="Základ006"
  Base = -> Box295
  Tool = -> Box293
FEATURE [Part::MultiFuse] Fusion005043005007002054  label="bez der006"
  Shapes = -> [Cut018020020009027020002003004004027004,Fusion005043005007002057]
FEATURE [Part::Cut] Cut018020020009027020002003004004027003
  Base = -> Fusion005043005007002054
  Tool = -> Fusion005043005007002063
FEATURE [Part::Cut] Cut018020020009027020002003004004027002  label="PCB004"
  Base = -> Cut018020020009027020002003004004027003
  Placement = pos=(0,-13,26) rot=(1,0,0;0rad)
  Tool = -> Fusion005043005007002066
FEATURE [Part::Feature] Fusion005043005007002067  label="Imbus009"
  Placement = pos=(31,0,31) rot=(0,0,1;0rad)
  shape: bbox 10.4 x 3 x 6.4 mm, 6 faces (baked)
FEATURE [Part::Feature] Fusion005043005007002068  label="Imbus010"
  Placement = pos=(31,0,0) rot=(0,0,1;0rad)
  shape: bbox 10.4 x 3 x 6.4 mm, 6 faces (baked)
FEATURE [Part::FeaturePython] Screw023  label="M4x25-Screw008"  # Fasteners workbench fastener (typed FeaturePython)
  Placement = pos=(47.5,49,45) rot=(0,-1,0;1.5708rad)
  diameter = 6
  invert = false
  length = 0
  matchOuter = false
  offset = 0
  thread = false
  type = 13
FEATURE [Part::Feature] Fusion005043005007002069  label="Imbus011"
  Placement = pos=(0,0,31) rot=(0,0,1;0rad)
  shape: bbox 10.4 x 3 x 6.4 mm, 6 faces (baked)
FEATURE [Part::MultiFuse] Fusion005043005007002064  label="diry027"
  Placement = pos=(0,0,0.5) rot=(0,0,1;0rad)
  Shapes = -> [Cylinder112024025003003006010004096,Cylinder112024025003003006010004112,Cylinder112024025003003006010004099,Cylinder112024025003003006010004117,Cylinder112024025003003006010004109,Screw023,Fusion005043005007002061,Box299,Box291,Box304,Box305,Box301,Box298,Box297,Fusion005043005007002062,Fusion005043005007002068,Fusion005043005007002067,Fusion005043005007002069]
FEATURE [Part::Cut] Cut018020020009027020002003004004027005  label="DE004"
  Base = -> Fusion005043005007002065
  Tool = -> Fusion005043005007002064
FEATURE [Part::Box] Box306  label="Krychle270"
  AttacherType = Attacher::AttachEngine3D
  Height = 28.5
  Length = 6
  Placement = pos=(-6,-15,20.5) rot=(0,0,1;0rad)
  Width = 78
FEATURE [Part::Cylinder] Cylinder112024025003003006010004118  label="Válec851"
  Angle = 360
  AttacherType = Attacher::AttachEngine3D
  Height = 10
  Placement = pos=(0,51.5,0) rot=(0,1,0;1.55334rad)
  Radius = 1.65
FEATURE [Part::Cylinder] Cylinder112024025003003006010004119  label="Válec852"
  Angle = 360
  AttacherType = Attacher::AttachEngine3D
  Height = 10
  Placement = pos=(0,0,11.5) rot=(0,1,0;1.55334rad)
  Radius = 1.65
FEATURE [Part::Cylinder] Cylinder112024025003003006010004120  label="Válec853"
  Angle = 360
  AttacherType = Attacher::AttachEngine3D
  Height = 10
  Placement = pos=(0,0,0) rot=(0,1,0;1.55334rad)
  Radius = 1.65
FEATURE [Part::Cylinder] Cylinder112024025003003006010004121  label="Válec854"
  Angle = 360
  AttacherType = Attacher::AttachEngine3D
  Height = 10
  Placement = pos=(0,52,11.5) rot=(0,1,0;1.55334rad)
  Radius = 1.65
FEATURE [Part::MultiFuse] Fusion005043005007002070  label="SM3"
  Shapes = -> [Cylinder112024025003003006010004118,Cylinder112024025003003006010004119,Cylinder112024025003003006010004120,Cylinder112024025003003006010004121]
FEATURE [Part::Cylinder] Cylinder112024025003003006010004122  label="Válec855"
  Angle = 360
  AttacherType = Attacher::AttachEngine3D
  Height = 3.1
  Placement = pos=(0,51.5,0) rot=(0,1,0;1.55334rad)
  Radius = 3
FEATURE [Part::Cylinder] Cylinder112024025003003006010004123  label="Válec856"
  Angle = 360
  AttacherType = Attacher::AttachEngine3D
  Height = 3.1
  Placement = pos=(0,0,11.5) rot=(0,1,0;1.55334rad)
  Radius = 3
FEATURE [Part::Cylinder] Cylinder112024025003003006010004124  label="Válec857"
  Angle = 360
  AttacherType = Attacher::AttachEngine3D
  Height = 3.1
  Placement = pos=(0,0,0) rot=(0,1,0;1.55334rad)
  Radius = 3
FEATURE [Part::Cylinder] Cylinder112024025003003006010004125  label="Válec858"
  Angle = 360
  AttacherType = Attacher::AttachEngine3D
  Height = 3.1
  Placement = pos=(0,52,11.5) rot=(0,1,0;1.55334rad)
  Radius = 3
FEATURE [Part::MultiFuse] Fusion005043005007002071  label="SM004"
  Placement = pos=(7,0,0) rot=(0,0,1;0rad)
  Shapes = -> [Cylinder112024025003003006010004122,Cylinder112024025003003006010004123,Cylinder112024025003003006010004124,Cylinder112024025003003006010004125]
FEATURE [Part::MultiFuse] Fusion005043005007002072  label="Isrouby"
  Placement = pos=(-10,1,28.5) rot=(0,0,1;0rad)
  Shapes = -> [Fusion005043005007002071,Fusion005043005007002070]
FEATURE [Part::Box] Box308  label="Osazeni"
  AttacherType = Attacher::AttachEngine3D
  Height = 4
  Length = 3
  Placement = pos=(-6,-15,20.5) rot=(0,0,1;0rad)
  Width = 78
FEATURE [Part::MultiFuse] Fusion005043005007002073  label="DecBase"
  Shapes = -> [Box306,Box296,Cut018020020009027020002003004004027005,Cut018020020009027020002003004004027002]
FEATURE [Part::Cylinder] Cylinder112024025003003006010004126  label="Válec859"
  Angle = 360
  AttacherType = Attacher::AttachEngine3D
  Height = 10
  Placement = pos=(-3,-7,42) rot=(0,0,1;0rad)
  Radius = 0.75
FEATURE [Part::Cylinder] Cylinder112024025003003006010004127  label="Válec860"
  Angle = 360
  AttacherType = Attacher::AttachEngine3D
  Height = 10
  Placement = pos=(-3,7,42) rot=(0,0,1;0rad)
  Radius = 0.75
FEATURE [Part::Box] Box309  label="Krychle272"
  AttacherType = Attacher::AttachEngine3D
  Height = 12
  Length = 7
  Placement = pos=(-12,1,60) rot=(0,1,0;0.523599rad)
  Width = 62
FEATURE [Part::Cylinder] Cylinder112024025003003006010004128  label="Válec861"
  Angle = 360
  AttacherType = Attacher::AttachEngine3D
  Height = 3.1
  Placement = pos=(0,52,11.5) rot=(0,1,0;1.55334rad)
  Radius = 3
FEATURE [Part::Cylinder] Cylinder112024025003003006010004129  label="Válec862"
  Angle = 360
  AttacherType = Attacher::AttachEngine3D
  Height = 10
  Placement = pos=(0,0,11.5) rot=(0,1,0;1.55334rad)
  Radius = 1.65
FEATURE [Part::Cylinder] Cylinder112024025003003006010004130  label="Válec863"
  Angle = 360
  AttacherType = Attacher::AttachEngine3D
  Height = 10
  Placement = pos=(0,52,11.5) rot=(0,1,0;1.55334rad)
  Radius = 1.65
FEATURE [Part::Cylinder] Cylinder112024025003003006010004131  label="Válec864"
  Angle = 360
  AttacherType = Attacher::AttachEngine3D
  Height = 10
  Placement = pos=(0,0,0) rot=(0,1,0;1.55334rad)
  Radius = 1.65
FEATURE [Part::Cylinder] Cylinder112024025003003006010004132  label="Válec865"
  Angle = 360
  AttacherType = Attacher::AttachEngine3D
  Height = 10
  Placement = pos=(0,52,0) rot=(0,1,0;1.55334rad)
  Radius = 1.65
FEATURE [Part::MultiFuse] Fusion005043005007002075  label="SM005"
  Shapes = -> [Cylinder112024025003003006010004132,Cylinder112024025003003006010004129,Cylinder112024025003003006010004131,Cylinder112024025003003006010004130]
FEATURE [Part::Cylinder] Cylinder112024025003003006010004133  label="Válec866"
  Angle = 360
  AttacherType = Attacher::AttachEngine3D
  Height = 3.1
  Placement = pos=(0,0,11.5) rot=(0,1,0;1.55334rad)
  Radius = 3
FEATURE [Part::Cylinder] Cylinder112024025003003006010004134  label="Válec867"
  Angle = 360
  AttacherType = Attacher::AttachEngine3D
  Height = 3.1
  Placement = pos=(0,52,0) rot=(0,1,0;1.55334rad)
  Radius = 3
FEATURE [Part::Cylinder] Cylinder112024025003003006010004135  label="Válec868"
  Angle = 360
  AttacherType = Attacher::AttachEngine3D
  Height = 3.1
  Placement = pos=(0,0,0) rot=(0,1,0;1.55334rad)
  Radius = 3
FEATURE [Part::MultiFuse] Fusion005043005007002077  label="SM006"
  Placement = pos=(7,0,0) rot=(0,0,1;0rad)
  Shapes = -> [Cylinder112024025003003006010004134,Cylinder112024025003003006010004133,Cylinder112024025003003006010004135,Cylinder112024025003003006010004128]
FEATURE [Part::MultiFuse] Fusion005043005007002076  label="Isrouby001"
  Placement = pos=(-10,1,28.5) rot=(0,0,1;0rad)
  Shapes = -> [Fusion005043005007002077,Fusion005043005007002075]
FEATURE [Part::Box] Box310  label="Krychle273"
  AttacherType = Attacher::AttachEngine3D
  Height = 22
  Length = 0.6
  Placement = pos=(1,-4,-7.5) rot=(0,0,1;0rad)
  Width = 71
FEATURE [Part::Cylinder] Cylinder112024025003003006010004136  label="Válec869"
  Angle = 360
  AttacherType = Attacher::AttachEngine3D
  Height = 10
  Placement = pos=(0,0,11.5) rot=(0,1,0;1.55334rad)
  Radius = 1.65
FEATURE [Part::Cylinder] Cylinder112024025003003006010004137  label="Válec870"
  Angle = 360
  AttacherType = Attacher::AttachEngine3D
  Height = 10
  Placement = pos=(0,52,11.5) rot=(0,1,0;1.55334rad)
  Radius = 1.65
FEATURE [Part::Cylinder] Cylinder112024025003003006010004138  label="Válec871"
  Angle = 360
  AttacherType = Attacher::AttachEngine3D
  Height = 10
  Placement = pos=(0,0,0) rot=(0,1,0;1.55334rad)
  Radius = 1.65
FEATURE [Part::Cylinder] Cylinder112024025003003006010004139  label="Válec872"
  Angle = 360
  AttacherType = Attacher::AttachEngine3D
  Height = 10
  Placement = pos=(0,52,0) rot=(0,1,0;1.55334rad)
  Radius = 1.65
FEATURE [Part::MultiFuse] Fusion005043005007002078  label="SM007"
  Shapes = -> [Cylinder112024025003003006010004139,Cylinder112024025003003006010004136,Cylinder112024025003003006010004138,Cylinder112024025003003006010004137]
FEATURE [Part::Cut] Cut018020020009027020002003004004027006002  label="Maska diry RA"
  Base = -> Box310
  Tool = -> Fusion005043005007002078
FEATURE [Part::FeaturePython] Screw024  label="M4x25-Screw009"  # Fasteners workbench fastener (typed FeaturePython)
  Placement = pos=(47.5,49,45) rot=(0,-1,0;1.5708rad)
  diameter = 6
  invert = false
  length = 0
  matchOuter = false
  offset = 0
  thread = false
  type = 13
FEATURE [Part::Part2DObjectPython] ShapeString026  # Draft 2D object (typed FeaturePython)
  FontFile = <path>
  Placement = pos=(15.3452,-2,30.5072) rot=(1,0,0;1.5708rad)
  Size = 0.01
  String = .
  Tracking = 0
FEATURE [Part::Part2DObjectPython] ShapeString027  # Draft 2D object (typed FeaturePython)
  FontFile = <path>
  Placement = pos=(15.3452,-2,30.5072) rot=(1,0,0;1.5708rad)
  Size = 4
  String = RA
  Tracking = 0
FEATURE [Part::Feature] Fusion005043005007002079  label="Imbus012"
  Placement = pos=(0,0,31) rot=(0,0,1;0rad)
  shape: bbox 10.4 x 3 x 6.4 mm, 6 faces (baked)
FEATURE [Part::Feature] Fusion005043005007002080  label="Imbus013"
  Placement = pos=(31,0,31) rot=(0,0,1;0rad)
  shape: bbox 10.4 x 3 x 6.4 mm, 6 faces (baked)
FEATURE [Part::Feature] Fusion005043005007002081  label="Imbus014"
  Placement = pos=(31,0,0) rot=(0,0,1;0rad)
  shape: bbox 10.4 x 3 x 6.4 mm, 6 faces (baked)
FEATURE [Part::Extrusion] Extrude096  label="Text TR007"
  Base = -> ShapeString026
  Dir = (0,-1,0)
  DirMode = 2
  FaceMakerClass = Part::FaceMakerBullseye
  LengthFwd = 1
  LengthRev = 0
  Placement = pos=(-6.75,0.5,-33) rot=(0,0,1;0rad)
  Solid = false
  Symmetric = false
FEATURE [Part::Box] Box311  label="RJ061"
  AttacherType = Attacher::AttachEngine3D
  Height = 13
  Length = 16
  Placement = pos=(32,-5,4.5) rot=(0,0,1;0rad)
  Width = 18.5
FEATURE [Part::Cylinder] Cylinder112024025003003006010004140  label="Válec873"
  Angle = 360
  AttacherType = Attacher::AttachEngine3D
  Height = 6.5
  Placement = pos=(53.5,21.25,0) rot=(0,0,1;0rad)
  Radius = 3.5
FEATURE [Part::Cylinder] Cylinder112024025003003006010004141  label="Válec874"
  Angle = 360
  AttacherType = Attacher::AttachEngine3D
  Height = 6.5
  Placement = pos=(53.5,6,0) rot=(0,0,1;0rad)
  Radius = 3.5
FEATURE [Part::Cylinder] Cylinder112024025003003006010004142  label="Válec875"
  Angle = 360
  AttacherType = Attacher::AttachEngine3D
  Height = 8
  Placement = pos=(53.5,21.25,0) rot=(0,0,1;0rad)
  Radius = 0.75
FEATURE [Part::Cylinder] Cylinder112024025003003006010004143  label="Válec876"
  Angle = 360
  AttacherType = Attacher::AttachEngine3D
  Height = 10
  Placement = pos=(8,64,29.5) rot=(1,0,0;1.5708rad)
  Radius = 1.65
FEATURE [Part::Box] Box312  label="Krychle274"
  AttacherType = Attacher::AttachEngine3D
  Height = 43
  Length = 4
  Placement = pos=(55.5,16,23) rot=(0,0,1;0rad)
  Width = 40
FEATURE [Part::Box] Box313  label="Krychle275"
  AttacherType = Attacher::AttachEngine3D
  Height = 3.3
  Length = 4
  Placement = pos=(8,56,27.85) rot=(0,0,1;0rad)
  Width = 8
FEATURE [Part::Cylinder] Cylinder112024025003003006010004144  label="Válec877"
  Angle = 360
  AttacherType = Attacher::AttachEngine3D
  Height = 5
  Placement = pos=(14.25,1,9.5) rot=(1,0,0;1.5708rad)
  Radius = 0.01
FEATURE [Part::Cylinder] Cylinder112024025003003006010004145  label="Válec878"
  Angle = 360
  AttacherType = Attacher::AttachEngine3D
  Height = 10
  Placement = pos=(8,64,60.5) rot=(1,0,0;1.5708rad)
  Radius = 1.65
FEATURE [Part::Cylinder] Cylinder112024025003003006010004146  label="Válec879"
  Angle = 360
  AttacherType = Attacher::AttachEngine3D
  Height = 10
  Placement = pos=(8,64,60.5) rot=(1,0,0;1.5708rad)
  Radius = 1.65
FEATURE [Part::Box] Box314  label="Krychle276"
  AttacherType = Attacher::AttachEngine3D
  Height = 26
  Length = 58
  Placement = pos=(-0.5,0,-3) rot=(0,0,1;0rad)
  Width = 29
FEATURE [Part::Extrusion] Extrude097  label="Text RA007"
  Base = -> ShapeString027
  Dir = (0,-1,0)
  DirMode = 2
  FaceMakerClass = Part::FaceMakerBullseye
  LengthFwd = 1
  LengthRev = 0
  Placement = pos=(40,1,43.5) rot=(0,1,0;3.14159rad)
  Solid = false
  Symmetric = false
FEATURE [Part::Cylinder] Cylinder112024025003003006010004147  label="Válec880"
  Angle = 360
  AttacherType = Attacher::AttachEngine3D
  Height = 8
  Placement = pos=(3.5,21.25,0) rot=(0,0,1;0rad)
  Radius = 0.75
FEATURE [Part::Cylinder] Cylinder112024025003003006010004148  label="Válec881"
  Angle = 360
  AttacherType = Attacher::AttachEngine3D
  Height = 6.5
  Placement = pos=(3.5,21.25,0) rot=(0,0,1;0rad)
  Radius = 3.5
FEATURE [Part::Cylinder] Cylinder112024025003003006010004149  label="Válec882"
  Angle = 360
  AttacherType = Attacher::AttachEngine3D
  Height = 8
  Placement = pos=(53.5,6,0) rot=(0,0,1;0rad)
  Radius = 0.75
FEATURE [Part::Box] Box315  label="Krychle277"
  AttacherType = Attacher::AttachEngine3D
  Height = 28
  Length = 62
  Placement = pos=(-2.5,-2,-5) rot=(0,0,1;0rad)
  Width = 31
FEATURE [Part::Cylinder] Cylinder112024025003003006010004150  label="Válec883"
  Angle = 360
  AttacherType = Attacher::AttachEngine3D
  Height = 70
  Placement = pos=(-5,20,16.5) rot=(0,1,0;1.5708rad)
  Radius = 1
FEATURE [Part::Cylinder] Cylinder112024025003003006010004151  label="Válec884"
  Angle = 360
  AttacherType = Attacher::AttachEngine3D
  Height = 6.5
  Placement = pos=(3.5,6,0) rot=(0,0,1;0rad)
  Radius = 3.5
FEATURE [Part::Box] Box316  label="Krychle278"
  AttacherType = Attacher::AttachEngine3D
  Height = 3
  Length = 62
  Placement = pos=(-2.5,-15,20.5) rot=(0,0,1;0rad)
  Width = 78
FEATURE [Part::Cylinder] Cylinder112024025003003006010004152  label="Válec885"
  Angle = 360
  AttacherType = Attacher::AttachEngine3D
  Height = 70
  Placement = pos=(-5,6,16.5) rot=(0,1,0;1.5708rad)
  Radius = 1
FEATURE [Part::Cylinder] Cylinder112024025003003006010004153  label="Válec886"
  Angle = 360
  AttacherType = Attacher::AttachEngine3D
  Height = 8
  Placement = pos=(3.5,6,0) rot=(0,0,1;0rad)
  Radius = 0.7
FEATURE [Part::Box] Box317  label="Krychle279"
  AttacherType = Attacher::AttachEngine3D
  Height = 43
  Length = 66
  Placement = pos=(-6,15.5,49.5) rot=(1,0,0;0.523599rad)
  Width = 48
FEATURE [Part::Cut] Cut018020020009027020002003004004027006006  label="Základ007"
  Base = -> Box315
  Tool = -> Box314
FEATURE [Part::MultiFuse] Fusion005043005007002082
  Shapes = -> [Extrude096,Extrude097]
FEATURE [Part::MultiFuse] Fusion005043005007002084  label="RJ a LED007"
  Shapes = -> [Box311,Cylinder112024025003003006010004144]
FEATURE [Part::MultiFuse] Fusion005043005007002091  label="diry028"
  Placement = pos=(0,0,-4) rot=(0,0,1;0rad)
  Shapes = -> [Cylinder112024025003003006010004147,Cylinder112024025003003006010004153,Cylinder112024025003003006010004142,Cylinder112024025003003006010004149]
FEATURE [Part::MultiFuse] Fusion005043005007002092  label="sloupky010"
  Placement = pos=(0,0,-3.5) rot=(0,0,1;0rad)
  Shapes = -> [Cylinder112024025003003006010004148,Cylinder112024025003003006010004151,Cylinder112024025003003006010004140,Cylinder112024025003003006010004141]
FEATURE [Part::MultiFuse] Fusion005043005007002083  label="bez der007"
  Shapes = -> [Cut018020020009027020002003004004027006006,Fusion005043005007002092]
FEATURE [Part::MultiFuse] Fusion005043005007002093  label="Horni diry016"
  Placement = pos=(0,0,3) rot=(0,0,1;0rad)
  Shapes = -> [Cylinder112024025003003006010004150,Cylinder112024025003003006010004152]
FEATURE [Part::MultiFuse] Fusion005043005007002094
  Shapes = -> [Fusion005043005007002091,Fusion005043005007002084,Fusion005043005007002093]
FEATURE [Part::Cut] Cut018020020009027020002003004004027006005
  Base = -> Fusion005043005007002083
  Tool = -> Fusion005043005007002094
FEATURE [Part::Cut] Cut018020020009027020002003004004027006003  label="PCB005"
  Base = -> Cut018020020009027020002003004004027006005
  Placement = pos=(0,-13,26) rot=(1,0,0;0rad)
  Tool = -> Fusion005043005007002082
FEATURE [Part::Cylinder] Cylinder112024025003003006010004154  label="Válec887"
  Angle = 360
  AttacherType = Attacher::AttachEngine3D
  Height = 3.1
  Placement = pos=(0,52.3,11.5) rot=(0,1,0;1.55334rad)
  Radius = 3
FEATURE [Part::Cylinder] Cylinder112024025003003006010004155  label="Válec888"
  Angle = 360
  AttacherType = Attacher::AttachEngine3D
  Height = 10
  Placement = pos=(0,0,11.5) rot=(0,1,0;1.55334rad)
  Radius = 1.65
FEATURE [Part::Cylinder] Cylinder112024025003003006010004156  label="Válec889"
  Angle = 360
  AttacherType = Attacher::AttachEngine3D
  Height = 10
  Placement = pos=(0,52.3,11.5) rot=(0,1,0;1.55334rad)
  Radius = 1.65
FEATURE [Part::Box] Box318  label="Krychle280"
  AttacherType = Attacher::AttachEngine3D
  Height = 25
  Length = 4
  Placement = pos=(23.5,56,32.5) rot=(0,0,1;0rad)
  Width = 8
FEATURE [Part::Box] Box319  label="Krychle281"
  AttacherType = Attacher::AttachEngine3D
  Height = 3.3
  Length = 4
  Placement = pos=(8,56,58.85) rot=(0,0,1;0rad)
  Width = 8
FEATURE [Part::Box] Box320  label="Krychle282"
  AttacherType = Attacher::AttachEngine3D
  Height = 3.3
  Length = 4
  Placement = pos=(39,56,58.85) rot=(0,0,1;0rad)
  Width = 8
FEATURE [Part::Cylinder] Cylinder112024025003003006010004157  label="Válec890"
  Angle = 360
  AttacherType = Attacher::AttachEngine3D
  Height = 10
  Placement = pos=(0,0,0) rot=(0,1,0;1.55334rad)
  Radius = 1.65
FEATURE [Part::Cylinder] Cylinder112024025003003006010004158  label="Válec891"
  Angle = 360
  AttacherType = Attacher::AttachEngine3D
  Height = 10
  Placement = pos=(0,51.7,0) rot=(0,1,0;1.55334rad)
  Radius = 1.65
FEATURE [Part::MultiFuse] Fusion005043005007002085  label="SM008"
  Shapes = -> [Cylinder112024025003003006010004158,Cylinder112024025003003006010004155,Cylinder112024025003003006010004157,Cylinder112024025003003006010004156]
FEATURE [Part::Box] Box321  label="Krychle283"
  AttacherType = Attacher::AttachEngine3D
  Height = 6.4
  Length = 4
  Placement = pos=(8,60,26.3) rot=(0,0,1;0rad)
  Width = 3
FEATURE [Part::Cylinder] Cylinder112024025003003006010004159  label="Válec892"
  Angle = 360
  AttacherType = Attacher::AttachEngine3D
  Height = 10
  Placement = pos=(39,64,29.5) rot=(1,0,0;1.5708rad)
  Radius = 1.65
FEATURE [Part::Cylinder] Cylinder112024025003003006010004160  label="Válec893"
  Angle = 360
  AttacherType = Attacher::AttachEngine3D
  Height = 3.1
  Placement = pos=(0,0,11.5) rot=(0,1,0;1.55334rad)
  Radius = 3
FEATURE [Part::Cylinder] Cylinder112024025003003006010004161  label="Válec894"
  Angle = 360
  AttacherType = Attacher::AttachEngine3D
  Height = 10
  Placement = pos=(8,64,29.5) rot=(1,0,0;1.5708rad)
  Radius = 1.65
FEATURE [Part::Box] Box322  label="konektor006"
  AttacherType = Attacher::AttachEngine3D
  Height = 29
  Length = 10
  Placement = pos=(50,16,37) rot=(0,0,1;0rad)
  Width = 12
FEATURE [Part::Cylinder] Cylinder112024025003003006010004162  label="Válec895"
  Angle = 360
  AttacherType = Attacher::AttachEngine3D
  Height = 3
  Placement = pos=(8,63,29.5) rot=(1,0,0;1.5708rad)
  Radius = 3.2
FEATURE [Part::Cylinder] Cylinder112024025003003006010004163  label="Válec896"
  Angle = 360
  AttacherType = Attacher::AttachEngine3D
  Height = 3.1
  Placement = pos=(0,51.7,0) rot=(0,1,0;1.55334rad)
  Radius = 3
FEATURE [Part::Box] Box323  label="Krychle284"
  AttacherType = Attacher::AttachEngine3D
  Height = 3.3
  Length = 4
  Placement = pos=(39,56,27.85) rot=(0,0,1;0rad)
  Width = 8
FEATURE [Part::Cylinder] Cylinder112024025003003006010004164  label="Válec897"
  Angle = 360
  AttacherType = Attacher::AttachEngine3D
  Height = 3.1
  Placement = pos=(0,0,0) rot=(0,1,0;1.55334rad)
  Radius = 3
FEATURE [Part::MultiFuse] Fusion005043005007002090  label="SM009"
  Placement = pos=(7,0,0) rot=(0,0,1;0rad)
  Shapes = -> [Cylinder112024025003003006010004163,Cylinder112024025003003006010004160,Cylinder112024025003003006010004164,Cylinder112024025003003006010004154]
FEATURE [Part::MultiFuse] Fusion005043005007002086  label="Isrouby002"
  Placement = pos=(-10,1,28.5) rot=(0,0,1;0rad)
  Shapes = -> [Fusion005043005007002090,Fusion005043005007002085]
FEATURE [Part::Box] Box324  label="Krychle285"
  AttacherType = Attacher::AttachEngine3D
  Height = 43
  Length = 59.5
  Placement = pos=(0,56,23) rot=(0,0,1;0rad)
  Width = 7
FEATURE [Part::Cylinder] Cylinder112024025003003006010004165  label="Válec898"
  Angle = 360
  AttacherType = Attacher::AttachEngine3D
  Height = 10
  Placement = pos=(39,64,29.5) rot=(1,0,0;1.5708rad)
  Radius = 1.65
FEATURE [Part::Cylinder] Cylinder112024025003003006010004166  label="Válec899"
  Angle = 360
  AttacherType = Attacher::AttachEngine3D
  Height = 20
  Placement = pos=(23.5,64,45) rot=(1,0,0;1.5708rad)
  Radius = 12.5
FEATURE [Part::Box] Box325  label="Krychle286"
  AttacherType = Attacher::AttachEngine3D
  Height = 43
  Length = 6
  Placement = pos=(-6,16,23) rot=(0,0,1;0rad)
  Width = 47
FEATURE [Part::MultiFuse] Fusion005043005007002088  label="Main006"
  Placement = pos=(0,0,0.5) rot=(0,0,1;0rad)
  Shapes = -> [Box324,Box312,Box325]
FEATURE [Part::Cylinder] Cylinder112024025003003006010004167  label="Válec900"
  Angle = 360
  AttacherType = Attacher::AttachEngine3D
  Height = 3
  Placement = pos=(12,63,29.5) rot=(1,0,0;1.5708rad)
  Radius = 3.2
FEATURE [Part::MultiFuse] Fusion005043005007002087  label="Imbus015"
  Shapes = -> [Cylinder112024025003003006010004167,Cylinder112024025003003006010004162,Box321]
FEATURE [Part::Cylinder] Cylinder112024025003003006010004168  label="Válec901"
  Angle = 360
  AttacherType = Attacher::AttachEngine3D
  Height = 10
  Placement = pos=(39,64,60.5) rot=(1,0,0;1.5708rad)
  Radius = 1.65
FEATURE [Part::Cylinder] Cylinder112024025003003006010004169  label="Válec902"
  Angle = 360
  AttacherType = Attacher::AttachEngine3D
  Height = 10
  Placement = pos=(39,64,60.5) rot=(1,0,0;1.5708rad)
  Radius = 1.65
FEATURE [Part::MultiFuse] Fusion005043005007002089
  Placement = pos=(4,0,0) rot=(0,0,1;0rad)
  Shapes = -> [Cylinder112024025003003006010004161,Cylinder112024025003003006010004145,Cylinder112024025003003006010004169,Cylinder112024025003003006010004166,Cylinder112024025003003006010004165]
FEATURE [Part::Box] Box326  label="Krychle287"
  AttacherType = Attacher::AttachEngine3D
  Height = 28.5
  Length = 6
  Placement = pos=(-6,-15,20.5) rot=(0,0,1;0rad)
  Width = 78
FEATURE [Part::Cylinder] Cylinder112024025003003006010004170  label="Válec903"
  Angle = 360
  AttacherType = Attacher::AttachEngine3D
  Height = 20
  Placement = pos=(23.5,64,45) rot=(1,0,0;1.5708rad)
  Radius = 12.5
FEATURE [Part::MultiFuse] Fusion005043005007002095  label="diry029"
  Placement = pos=(0,0,0.5) rot=(0,0,1;0rad)
  Shapes = -> [Cylinder112024025003003006010004143,Cylinder112024025003003006010004170,Cylinder112024025003003006010004146,Cylinder112024025003003006010004159,Cylinder112024025003003006010004168,Screw024,Fusion005043005007002089,Box318,Box313,Box320,Box323,Box319,Box322,Box317,Fusion005043005007002087,Fusion005043005007002081,Fusion005043005007002080,Fusion005043005007002079]
FEATURE [Part::Cut] Cut018020020009027020002003004004027006007  label="DE005"
  Base = -> Fusion005043005007002088
  Tool = -> Fusion005043005007002095
FEATURE [Part::MultiFuse] Fusion005043005007002097  label="DecBase001"
  Shapes = -> [Box326,Box316,Cut018020020009027020002003004004027006007,Cut018020020009027020002003004004027006003]
FEATURE [Part::Cylinder] Cylinder112024025003003006010004171  label="Válec904"
  Angle = 360
  AttacherType = Attacher::AttachEngine3D
  Height = 10
  Placement = pos=(-3,-7,42) rot=(0,0,1;0rad)
  Radius = 0.75
FEATURE [Part::Cylinder] Cylinder112024025003003006010004172  label="Válec905"
  Angle = 360
  AttacherType = Attacher::AttachEngine3D
  Height = 10
  Placement = pos=(-3,7,42) rot=(0,0,1;0rad)
  Radius = 0.75
FEATURE [Part::Part2DObjectPython] ShapeString  # Draft 2D object (typed FeaturePython)
  FontFile = <path>
  Placement = pos=(0,0,0) rot=(0,0,-1;1.5708rad)
  Size = 12
  String = OnStep
  Tracking = 0
FEATURE [Part::Extrusion] Extrude
  Base = -> ShapeString
  Dir = (0,0,1)
  DirMode = 2
  FaceMakerClass = Part::FaceMakerBullseye
  LengthFwd = 0.8
  LengthRev = 0
  Placement = pos=(21,52,21) rot=(0,1,0;3.14159rad)
  Solid = true
  Symmetric = false
FEATURE [Part::Part2DObjectPython] ShapeString028  # Draft 2D object (typed FeaturePython)
  FontFile = <path>
  Placement = pos=(0,0,0) rot=(0,0,-1;1.5708rad)
  Size = 12
  String = GS-280
  Tracking = 0
FEATURE [Part::Extrusion] Extrude098
  Base = -> ShapeString028
  Dir = (0,0,1)
  DirMode = 2
  FaceMakerClass = Part::FaceMakerBullseye
  LengthFwd = 0.8
  LengthRev = 0
  Placement = pos=(40,51,21) rot=(0,1,0;3.14159rad)
  Solid = true
  Symmetric = false
FEATURE [Part::MultiFuse] Fusion005043005007002098  label="Texty"
  Placement = pos=(5,0,0.3) rot=(0,0,1;0rad)
  Shapes = -> [Extrude,Extrude098]
FEATURE [Part::MultiFuse] Fusion005043005007002096
  Shapes = -> [Fusion005043005007002086,Cylinder112024025003003006010004171,Cylinder112024025003003006010004172,Fusion005043005007002098]
FEATURE [Part::Cut] Cut018020020009027020002003004004027006004  label="GS-280-RA"
  Base = -> Fusion005043005007002097
  Tool = -> Fusion005043005007002096
FEATURE [Part::Feature] Cut018020020009027020002003004004027006004002  label="Jezdec002"
  shape: bbox 49 x 12 x 43 mm, 24 faces (baked)
FEATURE [Part::FeaturePython] Screw025  label="M4x25-Screw010"  # Fasteners workbench fastener (typed FeaturePython)
  Placement = pos=(47.5,49,45) rot=(0,-1,0;1.5708rad)
  diameter = 6
  invert = false
  length = 0
  matchOuter = false
  offset = 0
  thread = false
  type = 13
FEATURE [Part::Box] Box327  label="Krychle288"
  AttacherType = Attacher::AttachEngine3D
  Height = 2
  Length = 65.5
  Placement = pos=(-6,-2,23) rot=(0,0,1;0rad)
  Width = 26
FEATURE [Part::Box] Box328  label="Krychle289"
  AttacherType = Attacher::AttachEngine3D
  Height = 8
  Length = 58
  Placement = pos=(-0.5,0,15) rot=(0,0,1;0rad)
  Width = 23
FEATURE [Part::MultiFuse] Fusion005043005007002099
  Shapes = -> [Box327,Box328]
FEATURE [Part::Box] Box329  label="Krychle290"
  AttacherType = Attacher::AttachEngine3D
  Height = 8
  Length = 54
  Placement = pos=(1.5,0,15) rot=(0,0,1;0rad)
  Width = 29
FEATURE [Part::Cylinder] Cylinder112024025003003006010004173  label="Válec906"
  Angle = 360
  AttacherType = Attacher::AttachEngine3D
  Height = 70
  Placement = pos=(-5,6,16.5) rot=(0,1,0;1.5708rad)
  Radius = 1
FEATURE [Part::Cylinder] Cylinder112024025003003006010004174  label="Válec907"
  Angle = 360
  AttacherType = Attacher::AttachEngine3D
  Height = 70
  Placement = pos=(-5,20,16.5) rot=(0,1,0;1.5708rad)
  Radius = 1
FEATURE [Part::MultiFuse] Fusion005043005007002100  label="Horni diry017"
  Placement = pos=(0,0,3) rot=(0,0,1;0rad)
  Shapes = -> [Cylinder112024025003003006010004174,Cylinder112024025003003006010004173]
FEATURE [Part::MultiFuse] Fusion005043005007002101
  Shapes = -> [Fusion005043005007002100,Box329]
FEATURE [Part::Cut] Cut018020020009027020002003004004027006004003
  Base = -> Fusion005043005007002099
  Tool = -> Fusion005043005007002101
FEATURE [Part::Part2DObjectPython] ShapeString029  # Draft 2D object (typed FeaturePython)
  FontFile = <path>
  Placement = pos=(15.3452,-2,30.5072) rot=(1,0,0;1.5708rad)
  Size = 10
  String = OnStep
  Tracking = 0
FEATURE [Part::Extrusion] Extrude099  label="OnStep006"
  Base = -> ShapeString029
  Dir = (0,-1,0)
  DirMode = 2
  FaceMakerClass = Part::FaceMakerBullseye
  LengthFwd = 1
  LengthRev = 0
  Placement = pos=(-11,-22,22) rot=(-1,0,0;1.5708rad)
  Solid = false
  Symmetric = false
FEATURE [Part::Cut] Cut018020020009027020002003004004027006004004  label="viko s texty006"
  Base = -> Cut018020020009027020002003004004027006004003
  Placement = pos=(0,-13,26) rot=(0,0,1;0rad)
  Tool = -> Extrude099
FEATURE [Part::Feature] Cut018020020009027020002003004004027006004005  label="Motor002"
  shape: bbox 48 x 57.1 x 42.3 mm, 100 faces (baked)
FEATURE [Part::Cylinder] Cylinder112024025003003006010004175  label="Válec908"
  Angle = 360
  AttacherType = Attacher::AttachEngine3D
  Height = 10
  Placement = pos=(-3,-7,42) rot=(0,0,1;0rad)
  Radius = 0.75
FEATURE [Part::Cylinder] Cylinder112024025003003006010004176  label="Válec909"
  Angle = 360
  AttacherType = Attacher::AttachEngine3D
  Height = 10
  Placement = pos=(-3,7,42) rot=(0,0,1;0rad)
  Radius = 0.75
FEATURE [Part::MultiFuse] Fusion005043005007002102
  Shapes = -> [Cylinder112024025003003006010004175,Cylinder112024025003003006010004176]
FEATURE [Part::Cut] Cut018020020009027020002003004004027006004006
  Base = -> Cut018020020009027020002003004004027006004004
  Tool = -> Fusion005043005007002102
FEATURE [Part::Chamfer] Chamfer008018  label="GS-280-CAP"
  Base = -> Cut018020020009027020002003004004027006004006
  Edges = 2 edges r=2: [Edge359,Edge366]
FEATURE [Part::Feature] Cut018020020009027020002003004004027006004007  label="GS-280-RA001"
  shape: bbox 65.56 x 78 x 46 mm, 425 faces (baked)
FEATURE [Part::Feature] Fillet001
  shape: bbox 56.29 x 56.29 x 15 mm, 29 faces (baked)
FEATURE [Part::Cylinder] Cylinder112024025003003006010004177  label="Válec910"
  Angle = 360
  AttacherType = Attacher::AttachEngine3D
  Height = 15
  Radius = 21
FEATURE [Part::Cylinder] Cylinder002  label="Válec002"
  Angle = 360
  AttacherType = Attacher::AttachEngine3D
  Height = 12
  Placement = pos=(0,0,3) rot=(0,0,1;0rad)
  Radius = 18
FEATURE [Part::Box] Box001  label="Krychle001"
  AttacherType = Attacher::AttachEngine3D
  Height = 12
  Length = 2
  Placement = pos=(-1,-21,3) rot=(0,0,1;0rad)
  Width = 42
FEATURE [Part::Cylinder] Cylinder001  label="Válec001"
  Angle = 360
  AttacherType = Attacher::AttachEngine3D
  Height = 3
  Radius = 26
FEATURE [Part::Box] Box330  label="Krychle291"
  AttacherType = Attacher::AttachEngine3D
  Height = 12
  Length = 42
  Placement = pos=(-21,-1,3) rot=(0,0,1;0rad)
  Width = 2
FEATURE [Part::MultiFuse] Fusion001
  Shapes = -> [Cylinder112024025003003006010004177,Cylinder001]
FEATURE [Part::MultiFuse] Fusion005043005007002103
  Shapes = -> [Cylinder002,Box330,Box001]
FEATURE [Part::Cut] Cut018020020009027020002003004004027006004008
  Base = -> Fusion001
  Tool = -> Fusion005043005007002103
FEATURE [Part::Fillet] Fillet004005003002003
  Base = -> Cut018020020009027020002003004004027006004008
  Edges = 6 edges r=1: [Edge4,Edge29,Edge31,Edge36,Edge41,Edge46]
FEATURE [App::Part] Part006  label="PollarCap"
  Group = -> [Fillet001,Box001,Cylinder112024025003003006010004177,Cylinder002,Cylinder001,Box330,Fusion005043005007002103,Fusion001,Cut018020020009027020002003004004027006004008,Fillet004005003002003]
  License = CC BY 3.0
  LicenseURL = http://creativecommons.org/licenses/by/3.0/
  Origin = -> Origin006
FEATURE [Part::Part2DObjectPython] ShapeString030  # Draft 2D object (typed FeaturePython)
  FontFile = <path>
  Placement = pos=(0,0,0) rot=(0,0,-1;1.5708rad)
  Size = 12
  String = OnStep
  Tracking = 0
FEATURE [Part::Part2DObjectPython] ShapeString031  # Draft 2D object (typed FeaturePython)
  FontFile = <path>
  Placement = pos=(0,0,0) rot=(0,0,-1;1.5708rad)
  Size = 12
  String = GS-280
  Tracking = 0
FEATURE [Part::Extrusion] Extrude100
  Base = -> ShapeString030
  Dir = (0,0,1)
  DirMode = 2
  FaceMakerClass = Part::FaceMakerBullseye
  LengthFwd = 0.8
  LengthRev = 0
  Placement = pos=(21,52,21) rot=(0,1,0;3.14159rad)
  Solid = true
  Symmetric = false
FEATURE [Part::Extrusion] Extrude101
  Base = -> ShapeString031
  Dir = (0,0,1)
  DirMode = 2
  FaceMakerClass = Part::FaceMakerBullseye
  LengthFwd = 0.8
  LengthRev = 0
  Placement = pos=(40,51,21) rot=(0,1,0;3.14159rad)
  Solid = true
  Symmetric = false
FEATURE [Part::MultiFuse] Fusion005043005007002104  label="Texty001"
  Placement = pos=(5,0,0.3) rot=(0,0,1;0rad)
  Shapes = -> [Extrude100,Extrude101]
FEATURE [Part::MultiFuse] Fusion005043005007002074
  Shapes = -> [Fusion005043005007002072,Box308,Cylinder112024025003003006010004126,Cylinder112024025003003006010004127,Box309,Fusion005043005007002104]
FEATURE [Part::Cut] Cut018020020009027020002003004004027006  label="GS-280-DEC"
  Base = -> Fusion005043005007002073
  Tool = -> Fusion005043005007002074
FEATURE [Part::Feature] Cut018020020009027020002003004004027006004009  label="GS-280-DEC002"
  shape: bbox 65.56 x 78 x 46 mm, 442 faces (baked)
FEATURE [App::Part] Part004  label="FIN GS-280"
  Group = -> [Cut018020020009027020002003004004027006003,Fusion005043005007002079,Fusion005043005007002081,Fusion005043005007002080,Extrude096,Cylinder112024025003003006010004142,Cylinder112024025003003006010004143,Box313,Cylinder112024025003003006010004144,Cylinder112024025003003006010004145,Cylinder112024025003003006010004146,Box314,Box312,Cylinder112024025003003006010004140,Box311,+183 more]
  Origin = -> Origin004
note: 21 file-system paths scrubbed to <path> (originals preserved in the JSON sidecar)
